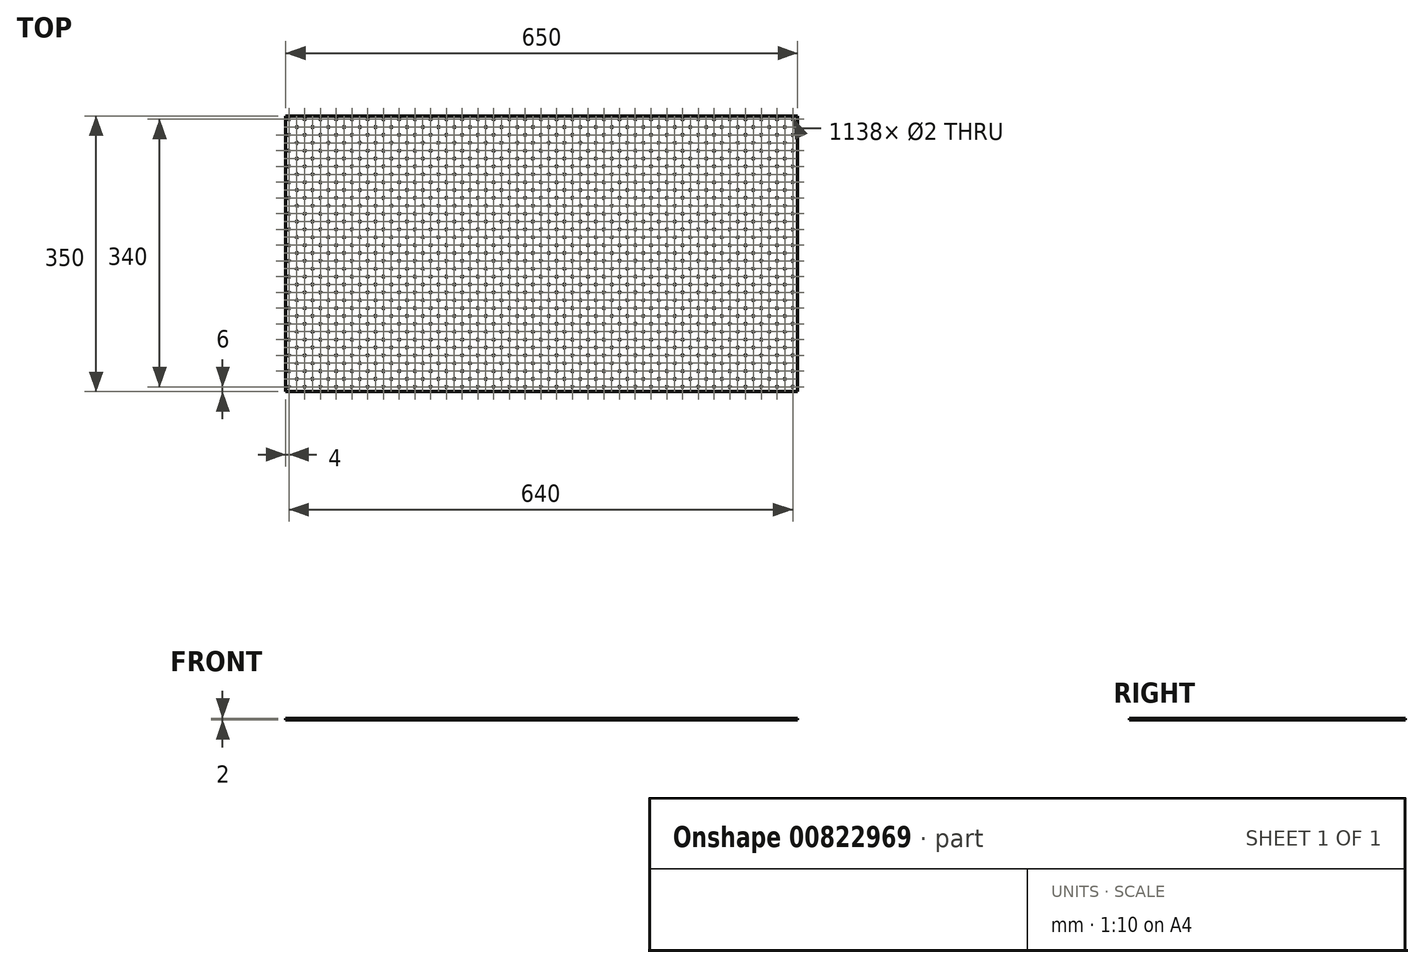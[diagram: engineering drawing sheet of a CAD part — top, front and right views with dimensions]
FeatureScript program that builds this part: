
annotation { "Feature Type Name" : "Feature", "Feature Type Description" : "" }
export const myFeature = defineFeature(function(context is Context, id is Id, definition is map)
    precondition{}
    {
        {
            var Q0;
            Q0=qCreatedBy(makeId("Top.planeOp"),FACE);
            var sketch = newSketch(context, id + "F0", { "sketchPlane" : qUnion([Q0])});
            skLineSegment(sketch, "E0.bottom", {"start": v(-325, -175) * mm, "end": v(325, -175) * mm});
            skLineSegment(sketch, "E0.top", {"start": v(-325, 175) * mm, "end": v(325, 175) * mm});
            skLineSegment(sketch, "E0.left", {"start": v(-325, -175) * mm, "end": v(-325, 175) * mm});
            skLineSegment(sketch, "E0.right", {"start": v(325, -175) * mm, "end": v(325, 175) * mm});
            skPoint(sketch, "E0.middle", {"position": v(0, 0) * mm});
            skCircle(sketch, "E1", {"center": v(-321, 171) * mm, "radius": 1 * mm});
            skCircle(sketch, "E2", {"center": v(-311, 161) * mm, "radius": 1 * mm});
            skCircle(sketch, "E3.0.1.0", {"center": v(-321, 151) * mm, "radius": 1 * mm});
            skCircle(sketch, "E3.0.1.1", {"center": v(-311, 141) * mm, "radius": 1 * mm});
            skCircle(sketch, "E3.0.2.0", {"center": v(-321, 131) * mm, "radius": 1 * mm});
            skCircle(sketch, "E3.0.2.1", {"center": v(-311, 121) * mm, "radius": 1 * mm});
            skCircle(sketch, "E3.0.3.0", {"center": v(-321, 111) * mm, "radius": 1 * mm});
            skCircle(sketch, "E3.0.3.1", {"center": v(-311, 101) * mm, "radius": 1 * mm});
            skCircle(sketch, "E3.0.4.0", {"center": v(-321, 91) * mm, "radius": 1 * mm});
            skCircle(sketch, "E3.0.4.1", {"center": v(-311, 81) * mm, "radius": 1 * mm});
            skCircle(sketch, "E3.0.5.0", {"center": v(-321, 71) * mm, "radius": 1 * mm});
            skCircle(sketch, "E3.0.5.1", {"center": v(-311, 61) * mm, "radius": 1 * mm});
            skCircle(sketch, "E3.0.6.0", {"center": v(-321, 51) * mm, "radius": 1 * mm});
            skCircle(sketch, "E3.0.6.1", {"center": v(-311, 41) * mm, "radius": 1 * mm});
            skCircle(sketch, "E3.0.7.0", {"center": v(-321, 31) * mm, "radius": 1 * mm});
            skCircle(sketch, "E3.0.7.1", {"center": v(-311, 21) * mm, "radius": 1 * mm});
            skCircle(sketch, "E3.0.8.0", {"center": v(-321, 11) * mm, "radius": 1 * mm});
            skCircle(sketch, "E3.0.8.1", {"center": v(-311, 1) * mm, "radius": 1 * mm});
            skCircle(sketch, "E3.0.9.0", {"center": v(-321, -9) * mm, "radius": 1 * mm});
            skCircle(sketch, "E3.0.9.1", {"center": v(-311, -19) * mm, "radius": 1 * mm});
            skCircle(sketch, "E3.0.10.0", {"center": v(-321, -29) * mm, "radius": 1 * mm});
            skCircle(sketch, "E3.0.10.1", {"center": v(-311, -39) * mm, "radius": 1 * mm});
            skCircle(sketch, "E3.0.11.0", {"center": v(-321, -49) * mm, "radius": 1 * mm});
            skCircle(sketch, "E3.0.11.1", {"center": v(-311, -59) * mm, "radius": 1 * mm});
            skCircle(sketch, "E3.0.12.0", {"center": v(-321, -69) * mm, "radius": 1 * mm});
            skCircle(sketch, "E3.0.12.1", {"center": v(-311, -79) * mm, "radius": 1 * mm});
            skCircle(sketch, "E3.0.13.0", {"center": v(-321, -89) * mm, "radius": 1 * mm});
            skCircle(sketch, "E3.0.13.1", {"center": v(-311, -99) * mm, "radius": 1 * mm});
            skCircle(sketch, "E3.0.14.0", {"center": v(-321, -109) * mm, "radius": 1 * mm});
            skCircle(sketch, "E3.0.14.1", {"center": v(-311, -119) * mm, "radius": 1 * mm});
            skCircle(sketch, "E3.0.15.0", {"center": v(-321, -129) * mm, "radius": 1 * mm});
            skCircle(sketch, "E3.0.15.1", {"center": v(-311, -139) * mm, "radius": 1 * mm});
            skCircle(sketch, "E3.0.16.0", {"center": v(-321, -149) * mm, "radius": 1 * mm});
            skCircle(sketch, "E3.0.16.1", {"center": v(-311, -159) * mm, "radius": 1 * mm});
            skCircle(sketch, "E3.0.17.0", {"center": v(-321, -169) * mm, "radius": 1 * mm});
            skCircle(sketch, "E3.0.17.1", {"center": v(-311, -179) * mm, "radius": 1 * mm, "construction": true});
            skCircle(sketch, "E3.1.0.0", {"center": v(-301, 171) * mm, "radius": 1 * mm});
            skCircle(sketch, "E3.1.0.1", {"center": v(-291, 161) * mm, "radius": 1 * mm});
            skCircle(sketch, "E3.1.1.0", {"center": v(-301, 151) * mm, "radius": 1 * mm});
            skCircle(sketch, "E3.1.1.1", {"center": v(-291, 141) * mm, "radius": 1 * mm});
            skCircle(sketch, "E3.1.2.0", {"center": v(-301, 131) * mm, "radius": 1 * mm});
            skCircle(sketch, "E3.1.2.1", {"center": v(-291, 121) * mm, "radius": 1 * mm});
            skCircle(sketch, "E3.1.3.0", {"center": v(-301, 111) * mm, "radius": 1 * mm});
            skCircle(sketch, "E3.1.3.1", {"center": v(-291, 101) * mm, "radius": 1 * mm});
            skCircle(sketch, "E3.1.4.0", {"center": v(-301, 91) * mm, "radius": 1 * mm});
            skCircle(sketch, "E3.1.4.1", {"center": v(-291, 81) * mm, "radius": 1 * mm});
            skCircle(sketch, "E3.1.5.0", {"center": v(-301, 71) * mm, "radius": 1 * mm});
            skCircle(sketch, "E3.1.5.1", {"center": v(-291, 61) * mm, "radius": 1 * mm});
            skCircle(sketch, "E3.1.6.0", {"center": v(-301, 51) * mm, "radius": 1 * mm});
            skCircle(sketch, "E3.1.6.1", {"center": v(-291, 41) * mm, "radius": 1 * mm});
            skCircle(sketch, "E3.1.7.0", {"center": v(-301, 31) * mm, "radius": 1 * mm});
            skCircle(sketch, "E3.1.7.1", {"center": v(-291, 21) * mm, "radius": 1 * mm});
            skCircle(sketch, "E3.1.8.0", {"center": v(-301, 11) * mm, "radius": 1 * mm});
            skCircle(sketch, "E3.1.8.1", {"center": v(-291, 1) * mm, "radius": 1 * mm});
            skCircle(sketch, "E3.1.9.0", {"center": v(-301, -9) * mm, "radius": 1 * mm});
            skCircle(sketch, "E3.1.9.1", {"center": v(-291, -19) * mm, "radius": 1 * mm});
            skCircle(sketch, "E3.1.10.0", {"center": v(-301, -29) * mm, "radius": 1 * mm});
            skCircle(sketch, "E3.1.10.1", {"center": v(-291, -39) * mm, "radius": 1 * mm});
            skCircle(sketch, "E3.1.11.0", {"center": v(-301, -49) * mm, "radius": 1 * mm});
            skCircle(sketch, "E3.1.11.1", {"center": v(-291, -59) * mm, "radius": 1 * mm});
            skCircle(sketch, "E3.1.12.0", {"center": v(-301, -69) * mm, "radius": 1 * mm});
            skCircle(sketch, "E3.1.12.1", {"center": v(-291, -79) * mm, "radius": 1 * mm});
            skCircle(sketch, "E3.1.13.0", {"center": v(-301, -89) * mm, "radius": 1 * mm});
            skCircle(sketch, "E3.1.13.1", {"center": v(-291, -99) * mm, "radius": 1 * mm});
            skCircle(sketch, "E3.1.14.0", {"center": v(-301, -109) * mm, "radius": 1 * mm});
            skCircle(sketch, "E3.1.14.1", {"center": v(-291, -119) * mm, "radius": 1 * mm});
            skCircle(sketch, "E3.1.15.0", {"center": v(-301, -129) * mm, "radius": 1 * mm});
            skCircle(sketch, "E3.1.15.1", {"center": v(-291, -139) * mm, "radius": 1 * mm});
            skCircle(sketch, "E3.1.16.0", {"center": v(-301, -149) * mm, "radius": 1 * mm});
            skCircle(sketch, "E3.1.16.1", {"center": v(-291, -159) * mm, "radius": 1 * mm});
            skCircle(sketch, "E3.1.17.0", {"center": v(-301, -169) * mm, "radius": 1 * mm});
            skCircle(sketch, "E3.1.17.1", {"center": v(-291, -179) * mm, "radius": 1 * mm, "construction": true});
            skCircle(sketch, "E3.2.0.0", {"center": v(-281, 171) * mm, "radius": 1 * mm});
            skCircle(sketch, "E3.2.0.1", {"center": v(-271, 161) * mm, "radius": 1 * mm});
            skCircle(sketch, "E3.2.1.0", {"center": v(-281, 151) * mm, "radius": 1 * mm});
            skCircle(sketch, "E3.2.1.1", {"center": v(-271, 141) * mm, "radius": 1 * mm});
            skCircle(sketch, "E3.2.2.0", {"center": v(-281, 131) * mm, "radius": 1 * mm});
            skCircle(sketch, "E3.2.2.1", {"center": v(-271, 121) * mm, "radius": 1 * mm});
            skCircle(sketch, "E3.2.3.0", {"center": v(-281, 111) * mm, "radius": 1 * mm});
            skCircle(sketch, "E3.2.3.1", {"center": v(-271, 101) * mm, "radius": 1 * mm});
            skCircle(sketch, "E3.2.4.0", {"center": v(-281, 91) * mm, "radius": 1 * mm});
            skCircle(sketch, "E3.2.4.1", {"center": v(-271, 81) * mm, "radius": 1 * mm});
            skCircle(sketch, "E3.2.5.0", {"center": v(-281, 71) * mm, "radius": 1 * mm});
            skCircle(sketch, "E3.2.5.1", {"center": v(-271, 61) * mm, "radius": 1 * mm});
            skCircle(sketch, "E3.2.6.0", {"center": v(-281, 51) * mm, "radius": 1 * mm});
            skCircle(sketch, "E3.2.6.1", {"center": v(-271, 41) * mm, "radius": 1 * mm});
            skCircle(sketch, "E3.2.7.0", {"center": v(-281, 31) * mm, "radius": 1 * mm});
            skCircle(sketch, "E3.2.7.1", {"center": v(-271, 21) * mm, "radius": 1 * mm});
            skCircle(sketch, "E3.2.8.0", {"center": v(-281, 11) * mm, "radius": 1 * mm});
            skCircle(sketch, "E3.2.8.1", {"center": v(-271, 1) * mm, "radius": 1 * mm});
            skCircle(sketch, "E3.2.9.0", {"center": v(-281, -9) * mm, "radius": 1 * mm});
            skCircle(sketch, "E3.2.9.1", {"center": v(-271, -19) * mm, "radius": 1 * mm});
            skCircle(sketch, "E3.2.10.0", {"center": v(-281, -29) * mm, "radius": 1 * mm});
            skCircle(sketch, "E3.2.10.1", {"center": v(-271, -39) * mm, "radius": 1 * mm});
            skCircle(sketch, "E3.2.11.0", {"center": v(-281, -49) * mm, "radius": 1 * mm});
            skCircle(sketch, "E3.2.11.1", {"center": v(-271, -59) * mm, "radius": 1 * mm});
            skCircle(sketch, "E3.2.12.0", {"center": v(-281, -69) * mm, "radius": 1 * mm});
            skCircle(sketch, "E3.2.12.1", {"center": v(-271, -79) * mm, "radius": 1 * mm});
            skCircle(sketch, "E3.2.13.0", {"center": v(-281, -89) * mm, "radius": 1 * mm});
            skCircle(sketch, "E3.2.13.1", {"center": v(-271, -99) * mm, "radius": 1 * mm});
            skCircle(sketch, "E3.2.14.0", {"center": v(-281, -109) * mm, "radius": 1 * mm});
            skCircle(sketch, "E3.2.14.1", {"center": v(-271, -119) * mm, "radius": 1 * mm});
            skCircle(sketch, "E3.2.15.0", {"center": v(-281, -129) * mm, "radius": 1 * mm});
            skCircle(sketch, "E3.2.15.1", {"center": v(-271, -139) * mm, "radius": 1 * mm});
            skCircle(sketch, "E3.2.16.0", {"center": v(-281, -149) * mm, "radius": 1 * mm});
            skCircle(sketch, "E3.2.16.1", {"center": v(-271, -159) * mm, "radius": 1 * mm});
            skCircle(sketch, "E3.2.17.0", {"center": v(-281, -169) * mm, "radius": 1 * mm});
            skCircle(sketch, "E3.2.17.1", {"center": v(-271, -179) * mm, "radius": 1 * mm, "construction": true});
            skCircle(sketch, "E3.3.0.0", {"center": v(-261, 171) * mm, "radius": 1 * mm});
            skCircle(sketch, "E3.3.0.1", {"center": v(-251, 161) * mm, "radius": 1 * mm});
            skCircle(sketch, "E3.3.1.0", {"center": v(-261, 151) * mm, "radius": 1 * mm});
            skCircle(sketch, "E3.3.1.1", {"center": v(-251, 141) * mm, "radius": 1 * mm});
            skCircle(sketch, "E3.3.2.0", {"center": v(-261, 131) * mm, "radius": 1 * mm});
            skCircle(sketch, "E3.3.2.1", {"center": v(-251, 121) * mm, "radius": 1 * mm});
            skCircle(sketch, "E3.3.3.0", {"center": v(-261, 111) * mm, "radius": 1 * mm});
            skCircle(sketch, "E3.3.3.1", {"center": v(-251, 101) * mm, "radius": 1 * mm});
            skCircle(sketch, "E3.3.4.0", {"center": v(-261, 91) * mm, "radius": 1 * mm});
            skCircle(sketch, "E3.3.4.1", {"center": v(-251, 81) * mm, "radius": 1 * mm});
            skCircle(sketch, "E3.3.5.0", {"center": v(-261, 71) * mm, "radius": 1 * mm});
            skCircle(sketch, "E3.3.5.1", {"center": v(-251, 61) * mm, "radius": 1 * mm});
            skCircle(sketch, "E3.3.6.0", {"center": v(-261, 51) * mm, "radius": 1 * mm});
            skCircle(sketch, "E3.3.6.1", {"center": v(-251, 41) * mm, "radius": 1 * mm});
            skCircle(sketch, "E3.3.7.0", {"center": v(-261, 31) * mm, "radius": 1 * mm});
            skCircle(sketch, "E3.3.7.1", {"center": v(-251, 21) * mm, "radius": 1 * mm});
            skCircle(sketch, "E3.3.8.0", {"center": v(-261, 11) * mm, "radius": 1 * mm});
            skCircle(sketch, "E3.3.8.1", {"center": v(-251, 1) * mm, "radius": 1 * mm});
            skCircle(sketch, "E3.3.9.0", {"center": v(-261, -9) * mm, "radius": 1 * mm});
            skCircle(sketch, "E3.3.9.1", {"center": v(-251, -19) * mm, "radius": 1 * mm});
            skCircle(sketch, "E3.3.10.0", {"center": v(-261, -29) * mm, "radius": 1 * mm});
            skCircle(sketch, "E3.3.10.1", {"center": v(-251, -39) * mm, "radius": 1 * mm});
            skCircle(sketch, "E3.3.11.0", {"center": v(-261, -49) * mm, "radius": 1 * mm});
            skCircle(sketch, "E3.3.11.1", {"center": v(-251, -59) * mm, "radius": 1 * mm});
            skCircle(sketch, "E3.3.12.0", {"center": v(-261, -69) * mm, "radius": 1 * mm});
            skCircle(sketch, "E3.3.12.1", {"center": v(-251, -79) * mm, "radius": 1 * mm});
            skCircle(sketch, "E3.3.13.0", {"center": v(-261, -89) * mm, "radius": 1 * mm});
            skCircle(sketch, "E3.3.13.1", {"center": v(-251, -99) * mm, "radius": 1 * mm});
            skCircle(sketch, "E3.3.14.0", {"center": v(-261, -109) * mm, "radius": 1 * mm});
            skCircle(sketch, "E3.3.14.1", {"center": v(-251, -119) * mm, "radius": 1 * mm});
            skCircle(sketch, "E3.3.15.0", {"center": v(-261, -129) * mm, "radius": 1 * mm});
            skCircle(sketch, "E3.3.15.1", {"center": v(-251, -139) * mm, "radius": 1 * mm});
            skCircle(sketch, "E3.3.16.0", {"center": v(-261, -149) * mm, "radius": 1 * mm});
            skCircle(sketch, "E3.3.16.1", {"center": v(-251, -159) * mm, "radius": 1 * mm});
            skCircle(sketch, "E3.3.17.0", {"center": v(-261, -169) * mm, "radius": 1 * mm});
            skCircle(sketch, "E3.3.17.1", {"center": v(-251, -179) * mm, "radius": 1 * mm, "construction": true});
            skCircle(sketch, "E3.4.0.0", {"center": v(-241, 171) * mm, "radius": 1 * mm});
            skCircle(sketch, "E3.4.0.1", {"center": v(-231, 161) * mm, "radius": 1 * mm});
            skCircle(sketch, "E3.4.1.0", {"center": v(-241, 151) * mm, "radius": 1 * mm});
            skCircle(sketch, "E3.4.1.1", {"center": v(-231, 141) * mm, "radius": 1 * mm});
            skCircle(sketch, "E3.4.2.0", {"center": v(-241, 131) * mm, "radius": 1 * mm});
            skCircle(sketch, "E3.4.2.1", {"center": v(-231, 121) * mm, "radius": 1 * mm});
            skCircle(sketch, "E3.4.3.0", {"center": v(-241, 111) * mm, "radius": 1 * mm});
            skCircle(sketch, "E3.4.3.1", {"center": v(-231, 101) * mm, "radius": 1 * mm});
            skCircle(sketch, "E3.4.4.0", {"center": v(-241, 91) * mm, "radius": 1 * mm});
            skCircle(sketch, "E3.4.4.1", {"center": v(-231, 81) * mm, "radius": 1 * mm});
            skCircle(sketch, "E3.4.5.0", {"center": v(-241, 71) * mm, "radius": 1 * mm});
            skCircle(sketch, "E3.4.5.1", {"center": v(-231, 61) * mm, "radius": 1 * mm});
            skCircle(sketch, "E3.4.6.0", {"center": v(-241, 51) * mm, "radius": 1 * mm});
            skCircle(sketch, "E3.4.6.1", {"center": v(-231, 41) * mm, "radius": 1 * mm});
            skCircle(sketch, "E3.4.7.0", {"center": v(-241, 31) * mm, "radius": 1 * mm});
            skCircle(sketch, "E3.4.7.1", {"center": v(-231, 21) * mm, "radius": 1 * mm});
            skCircle(sketch, "E3.4.8.0", {"center": v(-241, 11) * mm, "radius": 1 * mm});
            skCircle(sketch, "E3.4.8.1", {"center": v(-231, 1) * mm, "radius": 1 * mm});
            skCircle(sketch, "E3.4.9.0", {"center": v(-241, -9) * mm, "radius": 1 * mm});
            skCircle(sketch, "E3.4.9.1", {"center": v(-231, -19) * mm, "radius": 1 * mm});
            skCircle(sketch, "E3.4.10.0", {"center": v(-241, -29) * mm, "radius": 1 * mm});
            skCircle(sketch, "E3.4.10.1", {"center": v(-231, -39) * mm, "radius": 1 * mm});
            skCircle(sketch, "E3.4.11.0", {"center": v(-241, -49) * mm, "radius": 1 * mm});
            skCircle(sketch, "E3.4.11.1", {"center": v(-231, -59) * mm, "radius": 1 * mm});
            skCircle(sketch, "E3.4.12.0", {"center": v(-241, -69) * mm, "radius": 1 * mm});
            skCircle(sketch, "E3.4.12.1", {"center": v(-231, -79) * mm, "radius": 1 * mm});
            skCircle(sketch, "E3.4.13.0", {"center": v(-241, -89) * mm, "radius": 1 * mm});
            skCircle(sketch, "E3.4.13.1", {"center": v(-231, -99) * mm, "radius": 1 * mm});
            skCircle(sketch, "E3.4.14.0", {"center": v(-241, -109) * mm, "radius": 1 * mm});
            skCircle(sketch, "E3.4.14.1", {"center": v(-231, -119) * mm, "radius": 1 * mm});
            skCircle(sketch, "E3.4.15.0", {"center": v(-241, -129) * mm, "radius": 1 * mm});
            skCircle(sketch, "E3.4.15.1", {"center": v(-231, -139) * mm, "radius": 1 * mm});
            skCircle(sketch, "E3.4.16.0", {"center": v(-241, -149) * mm, "radius": 1 * mm});
            skCircle(sketch, "E3.4.16.1", {"center": v(-231, -159) * mm, "radius": 1 * mm});
            skCircle(sketch, "E3.4.17.0", {"center": v(-241, -169) * mm, "radius": 1 * mm});
            skCircle(sketch, "E3.4.17.1", {"center": v(-231, -179) * mm, "radius": 1 * mm, "construction": true});
            skCircle(sketch, "E3.5.0.0", {"center": v(-221, 171) * mm, "radius": 1 * mm});
            skCircle(sketch, "E3.5.0.1", {"center": v(-211, 161) * mm, "radius": 1 * mm});
            skCircle(sketch, "E3.5.1.0", {"center": v(-221, 151) * mm, "radius": 1 * mm});
            skCircle(sketch, "E3.5.1.1", {"center": v(-211, 141) * mm, "radius": 1 * mm});
            skCircle(sketch, "E3.5.2.0", {"center": v(-221, 131) * mm, "radius": 1 * mm});
            skCircle(sketch, "E3.5.2.1", {"center": v(-211, 121) * mm, "radius": 1 * mm});
            skCircle(sketch, "E3.5.3.0", {"center": v(-221, 111) * mm, "radius": 1 * mm});
            skCircle(sketch, "E3.5.3.1", {"center": v(-211, 101) * mm, "radius": 1 * mm});
            skCircle(sketch, "E3.5.4.0", {"center": v(-221, 91) * mm, "radius": 1 * mm});
            skCircle(sketch, "E3.5.4.1", {"center": v(-211, 81) * mm, "radius": 1 * mm});
            skCircle(sketch, "E3.5.5.0", {"center": v(-221, 71) * mm, "radius": 1 * mm});
            skCircle(sketch, "E3.5.5.1", {"center": v(-211, 61) * mm, "radius": 1 * mm});
            skCircle(sketch, "E3.5.6.0", {"center": v(-221, 51) * mm, "radius": 1 * mm});
            skCircle(sketch, "E3.5.6.1", {"center": v(-211, 41) * mm, "radius": 1 * mm});
            skCircle(sketch, "E3.5.7.0", {"center": v(-221, 31) * mm, "radius": 1 * mm});
            skCircle(sketch, "E3.5.7.1", {"center": v(-211, 21) * mm, "radius": 1 * mm});
            skCircle(sketch, "E3.5.8.0", {"center": v(-221, 11) * mm, "radius": 1 * mm});
            skCircle(sketch, "E3.5.8.1", {"center": v(-211, 1) * mm, "radius": 1 * mm});
            skCircle(sketch, "E3.5.9.0", {"center": v(-221, -9) * mm, "radius": 1 * mm});
            skCircle(sketch, "E3.5.9.1", {"center": v(-211, -19) * mm, "radius": 1 * mm});
            skCircle(sketch, "E3.5.10.0", {"center": v(-221, -29) * mm, "radius": 1 * mm});
            skCircle(sketch, "E3.5.10.1", {"center": v(-211, -39) * mm, "radius": 1 * mm});
            skCircle(sketch, "E3.5.11.0", {"center": v(-221, -49) * mm, "radius": 1 * mm});
            skCircle(sketch, "E3.5.11.1", {"center": v(-211, -59) * mm, "radius": 1 * mm});
            skCircle(sketch, "E3.5.12.0", {"center": v(-221, -69) * mm, "radius": 1 * mm});
            skCircle(sketch, "E3.5.12.1", {"center": v(-211, -79) * mm, "radius": 1 * mm});
            skCircle(sketch, "E3.5.13.0", {"center": v(-221, -89) * mm, "radius": 1 * mm});
            skCircle(sketch, "E3.5.13.1", {"center": v(-211, -99) * mm, "radius": 1 * mm});
            skCircle(sketch, "E3.5.14.0", {"center": v(-221, -109) * mm, "radius": 1 * mm});
            skCircle(sketch, "E3.5.14.1", {"center": v(-211, -119) * mm, "radius": 1 * mm});
            skCircle(sketch, "E3.5.15.0", {"center": v(-221, -129) * mm, "radius": 1 * mm});
            skCircle(sketch, "E3.5.15.1", {"center": v(-211, -139) * mm, "radius": 1 * mm});
            skCircle(sketch, "E3.5.16.0", {"center": v(-221, -149) * mm, "radius": 1 * mm});
            skCircle(sketch, "E3.5.16.1", {"center": v(-211, -159) * mm, "radius": 1 * mm});
            skCircle(sketch, "E3.5.17.0", {"center": v(-221, -169) * mm, "radius": 1 * mm});
            skCircle(sketch, "E3.5.17.1", {"center": v(-211, -179) * mm, "radius": 1 * mm, "construction": true});
            skCircle(sketch, "E3.6.0.0", {"center": v(-201, 171) * mm, "radius": 1 * mm});
            skCircle(sketch, "E3.6.0.1", {"center": v(-191, 161) * mm, "radius": 1 * mm});
            skCircle(sketch, "E3.6.1.0", {"center": v(-201, 151) * mm, "radius": 1 * mm});
            skCircle(sketch, "E3.6.1.1", {"center": v(-191, 141) * mm, "radius": 1 * mm});
            skCircle(sketch, "E3.6.2.0", {"center": v(-201, 131) * mm, "radius": 1 * mm});
            skCircle(sketch, "E3.6.2.1", {"center": v(-191, 121) * mm, "radius": 1 * mm});
            skCircle(sketch, "E3.6.3.0", {"center": v(-201, 111) * mm, "radius": 1 * mm});
            skCircle(sketch, "E3.6.3.1", {"center": v(-191, 101) * mm, "radius": 1 * mm});
            skCircle(sketch, "E3.6.4.0", {"center": v(-201, 91) * mm, "radius": 1 * mm});
            skCircle(sketch, "E3.6.4.1", {"center": v(-191, 81) * mm, "radius": 1 * mm});
            skCircle(sketch, "E3.6.5.0", {"center": v(-201, 71) * mm, "radius": 1 * mm});
            skCircle(sketch, "E3.6.5.1", {"center": v(-191, 61) * mm, "radius": 1 * mm});
            skCircle(sketch, "E3.6.6.0", {"center": v(-201, 51) * mm, "radius": 1 * mm});
            skCircle(sketch, "E3.6.6.1", {"center": v(-191, 41) * mm, "radius": 1 * mm});
            skCircle(sketch, "E3.6.7.0", {"center": v(-201, 31) * mm, "radius": 1 * mm});
            skCircle(sketch, "E3.6.7.1", {"center": v(-191, 21) * mm, "radius": 1 * mm});
            skCircle(sketch, "E3.6.8.0", {"center": v(-201, 11) * mm, "radius": 1 * mm});
            skCircle(sketch, "E3.6.8.1", {"center": v(-191, 1) * mm, "radius": 1 * mm});
            skCircle(sketch, "E3.6.9.0", {"center": v(-201, -9) * mm, "radius": 1 * mm});
            skCircle(sketch, "E3.6.9.1", {"center": v(-191, -19) * mm, "radius": 1 * mm});
            skCircle(sketch, "E3.6.10.0", {"center": v(-201, -29) * mm, "radius": 1 * mm});
            skCircle(sketch, "E3.6.10.1", {"center": v(-191, -39) * mm, "radius": 1 * mm});
            skCircle(sketch, "E3.6.11.0", {"center": v(-201, -49) * mm, "radius": 1 * mm});
            skCircle(sketch, "E3.6.11.1", {"center": v(-191, -59) * mm, "radius": 1 * mm});
            skCircle(sketch, "E3.6.12.0", {"center": v(-201, -69) * mm, "radius": 1 * mm});
            skCircle(sketch, "E3.6.12.1", {"center": v(-191, -79) * mm, "radius": 1 * mm});
            skCircle(sketch, "E3.6.13.0", {"center": v(-201, -89) * mm, "radius": 1 * mm});
            skCircle(sketch, "E3.6.13.1", {"center": v(-191, -99) * mm, "radius": 1 * mm});
            skCircle(sketch, "E3.6.14.0", {"center": v(-201, -109) * mm, "radius": 1 * mm});
            skCircle(sketch, "E3.6.14.1", {"center": v(-191, -119) * mm, "radius": 1 * mm});
            skCircle(sketch, "E3.6.15.0", {"center": v(-201, -129) * mm, "radius": 1 * mm});
            skCircle(sketch, "E3.6.15.1", {"center": v(-191, -139) * mm, "radius": 1 * mm});
            skCircle(sketch, "E3.6.16.0", {"center": v(-201, -149) * mm, "radius": 1 * mm});
            skCircle(sketch, "E3.6.16.1", {"center": v(-191, -159) * mm, "radius": 1 * mm});
            skCircle(sketch, "E3.6.17.0", {"center": v(-201, -169) * mm, "radius": 1 * mm});
            skCircle(sketch, "E3.6.17.1", {"center": v(-191, -179) * mm, "radius": 1 * mm, "construction": true});
            skCircle(sketch, "E3.7.0.0", {"center": v(-181, 171) * mm, "radius": 1 * mm});
            skCircle(sketch, "E3.7.0.1", {"center": v(-171, 161) * mm, "radius": 1 * mm});
            skCircle(sketch, "E3.7.1.0", {"center": v(-181, 151) * mm, "radius": 1 * mm});
            skCircle(sketch, "E3.7.1.1", {"center": v(-171, 141) * mm, "radius": 1 * mm});
            skCircle(sketch, "E3.7.2.0", {"center": v(-181, 131) * mm, "radius": 1 * mm});
            skCircle(sketch, "E3.7.2.1", {"center": v(-171, 121) * mm, "radius": 1 * mm});
            skCircle(sketch, "E3.7.3.0", {"center": v(-181, 111) * mm, "radius": 1 * mm});
            skCircle(sketch, "E3.7.3.1", {"center": v(-171, 101) * mm, "radius": 1 * mm});
            skCircle(sketch, "E3.7.4.0", {"center": v(-181, 91) * mm, "radius": 1 * mm});
            skCircle(sketch, "E3.7.4.1", {"center": v(-171, 81) * mm, "radius": 1 * mm});
            skCircle(sketch, "E3.7.5.0", {"center": v(-181, 71) * mm, "radius": 1 * mm});
            skCircle(sketch, "E3.7.5.1", {"center": v(-171, 61) * mm, "radius": 1 * mm});
            skCircle(sketch, "E3.7.6.0", {"center": v(-181, 51) * mm, "radius": 1 * mm});
            skCircle(sketch, "E3.7.6.1", {"center": v(-171, 41) * mm, "radius": 1 * mm});
            skCircle(sketch, "E3.7.7.0", {"center": v(-181, 31) * mm, "radius": 1 * mm});
            skCircle(sketch, "E3.7.7.1", {"center": v(-171, 21) * mm, "radius": 1 * mm});
            skCircle(sketch, "E3.7.8.0", {"center": v(-181, 11) * mm, "radius": 1 * mm});
            skCircle(sketch, "E3.7.8.1", {"center": v(-171, 1) * mm, "radius": 1 * mm});
            skCircle(sketch, "E3.7.9.0", {"center": v(-181, -9) * mm, "radius": 1 * mm});
            skCircle(sketch, "E3.7.9.1", {"center": v(-171, -19) * mm, "radius": 1 * mm});
            skCircle(sketch, "E3.7.10.0", {"center": v(-181, -29) * mm, "radius": 1 * mm});
            skCircle(sketch, "E3.7.10.1", {"center": v(-171, -39) * mm, "radius": 1 * mm});
            skCircle(sketch, "E3.7.11.0", {"center": v(-181, -49) * mm, "radius": 1 * mm});
            skCircle(sketch, "E3.7.11.1", {"center": v(-171, -59) * mm, "radius": 1 * mm});
            skCircle(sketch, "E3.7.12.0", {"center": v(-181, -69) * mm, "radius": 1 * mm});
            skCircle(sketch, "E3.7.12.1", {"center": v(-171, -79) * mm, "radius": 1 * mm});
            skCircle(sketch, "E3.7.13.0", {"center": v(-181, -89) * mm, "radius": 1 * mm});
            skCircle(sketch, "E3.7.13.1", {"center": v(-171, -99) * mm, "radius": 1 * mm});
            skCircle(sketch, "E3.7.14.0", {"center": v(-181, -109) * mm, "radius": 1 * mm});
            skCircle(sketch, "E3.7.14.1", {"center": v(-171, -119) * mm, "radius": 1 * mm});
            skCircle(sketch, "E3.7.15.0", {"center": v(-181, -129) * mm, "radius": 1 * mm});
            skCircle(sketch, "E3.7.15.1", {"center": v(-171, -139) * mm, "radius": 1 * mm});
            skCircle(sketch, "E3.7.16.0", {"center": v(-181, -149) * mm, "radius": 1 * mm});
            skCircle(sketch, "E3.7.16.1", {"center": v(-171, -159) * mm, "radius": 1 * mm});
            skCircle(sketch, "E3.7.17.0", {"center": v(-181, -169) * mm, "radius": 1 * mm});
            skCircle(sketch, "E3.7.17.1", {"center": v(-171, -179) * mm, "radius": 1 * mm, "construction": true});
            skCircle(sketch, "E3.8.0.0", {"center": v(-161, 171) * mm, "radius": 1 * mm});
            skCircle(sketch, "E3.8.0.1", {"center": v(-151, 161) * mm, "radius": 1 * mm});
            skCircle(sketch, "E3.8.1.0", {"center": v(-161, 151) * mm, "radius": 1 * mm});
            skCircle(sketch, "E3.8.1.1", {"center": v(-151, 141) * mm, "radius": 1 * mm});
            skCircle(sketch, "E3.8.2.0", {"center": v(-161, 131) * mm, "radius": 1 * mm});
            skCircle(sketch, "E3.8.2.1", {"center": v(-151, 121) * mm, "radius": 1 * mm});
            skCircle(sketch, "E3.8.3.0", {"center": v(-161, 111) * mm, "radius": 1 * mm});
            skCircle(sketch, "E3.8.3.1", {"center": v(-151, 101) * mm, "radius": 1 * mm});
            skCircle(sketch, "E3.8.4.0", {"center": v(-161, 91) * mm, "radius": 1 * mm});
            skCircle(sketch, "E3.8.4.1", {"center": v(-151, 81) * mm, "radius": 1 * mm});
            skCircle(sketch, "E3.8.5.0", {"center": v(-161, 71) * mm, "radius": 1 * mm});
            skCircle(sketch, "E3.8.5.1", {"center": v(-151, 61) * mm, "radius": 1 * mm});
            skCircle(sketch, "E3.8.6.0", {"center": v(-161, 51) * mm, "radius": 1 * mm});
            skCircle(sketch, "E3.8.6.1", {"center": v(-151, 41) * mm, "radius": 1 * mm});
            skCircle(sketch, "E3.8.7.0", {"center": v(-161, 31) * mm, "radius": 1 * mm});
            skCircle(sketch, "E3.8.7.1", {"center": v(-151, 21) * mm, "radius": 1 * mm});
            skCircle(sketch, "E3.8.8.0", {"center": v(-161, 11) * mm, "radius": 1 * mm});
            skCircle(sketch, "E3.8.8.1", {"center": v(-151, 1) * mm, "radius": 1 * mm});
            skCircle(sketch, "E3.8.9.0", {"center": v(-161, -9) * mm, "radius": 1 * mm});
            skCircle(sketch, "E3.8.9.1", {"center": v(-151, -19) * mm, "radius": 1 * mm});
            skCircle(sketch, "E3.8.10.0", {"center": v(-161, -29) * mm, "radius": 1 * mm});
            skCircle(sketch, "E3.8.10.1", {"center": v(-151, -39) * mm, "radius": 1 * mm});
            skCircle(sketch, "E3.8.11.0", {"center": v(-161, -49) * mm, "radius": 1 * mm});
            skCircle(sketch, "E3.8.11.1", {"center": v(-151, -59) * mm, "radius": 1 * mm});
            skCircle(sketch, "E3.8.12.0", {"center": v(-161, -69) * mm, "radius": 1 * mm});
            skCircle(sketch, "E3.8.12.1", {"center": v(-151, -79) * mm, "radius": 1 * mm});
            skCircle(sketch, "E3.8.13.0", {"center": v(-161, -89) * mm, "radius": 1 * mm});
            skCircle(sketch, "E3.8.13.1", {"center": v(-151, -99) * mm, "radius": 1 * mm});
            skCircle(sketch, "E3.8.14.0", {"center": v(-161, -109) * mm, "radius": 1 * mm});
            skCircle(sketch, "E3.8.14.1", {"center": v(-151, -119) * mm, "radius": 1 * mm});
            skCircle(sketch, "E3.8.15.0", {"center": v(-161, -129) * mm, "radius": 1 * mm});
            skCircle(sketch, "E3.8.15.1", {"center": v(-151, -139) * mm, "radius": 1 * mm});
            skCircle(sketch, "E3.8.16.0", {"center": v(-161, -149) * mm, "radius": 1 * mm});
            skCircle(sketch, "E3.8.16.1", {"center": v(-151, -159) * mm, "radius": 1 * mm});
            skCircle(sketch, "E3.8.17.0", {"center": v(-161, -169) * mm, "radius": 1 * mm});
            skCircle(sketch, "E3.8.17.1", {"center": v(-151, -179) * mm, "radius": 1 * mm, "construction": true});
            skCircle(sketch, "E3.9.0.0", {"center": v(-141, 171) * mm, "radius": 1 * mm});
            skCircle(sketch, "E3.9.0.1", {"center": v(-131, 161) * mm, "radius": 1 * mm});
            skCircle(sketch, "E3.9.1.0", {"center": v(-141, 151) * mm, "radius": 1 * mm});
            skCircle(sketch, "E3.9.1.1", {"center": v(-131, 141) * mm, "radius": 1 * mm});
            skCircle(sketch, "E3.9.2.0", {"center": v(-141, 131) * mm, "radius": 1 * mm});
            skCircle(sketch, "E3.9.2.1", {"center": v(-131, 121) * mm, "radius": 1 * mm});
            skCircle(sketch, "E3.9.3.0", {"center": v(-141, 111) * mm, "radius": 1 * mm});
            skCircle(sketch, "E3.9.3.1", {"center": v(-131, 101) * mm, "radius": 1 * mm});
            skCircle(sketch, "E3.9.4.0", {"center": v(-141, 91) * mm, "radius": 1 * mm});
            skCircle(sketch, "E3.9.4.1", {"center": v(-131, 81) * mm, "radius": 1 * mm});
            skCircle(sketch, "E3.9.5.0", {"center": v(-141, 71) * mm, "radius": 1 * mm});
            skCircle(sketch, "E3.9.5.1", {"center": v(-131, 61) * mm, "radius": 1 * mm});
            skCircle(sketch, "E3.9.6.0", {"center": v(-141, 51) * mm, "radius": 1 * mm});
            skCircle(sketch, "E3.9.6.1", {"center": v(-131, 41) * mm, "radius": 1 * mm});
            skCircle(sketch, "E3.9.7.0", {"center": v(-141, 31) * mm, "radius": 1 * mm});
            skCircle(sketch, "E3.9.7.1", {"center": v(-131, 21) * mm, "radius": 1 * mm});
            skCircle(sketch, "E3.9.8.0", {"center": v(-141, 11) * mm, "radius": 1 * mm});
            skCircle(sketch, "E3.9.8.1", {"center": v(-131, 1) * mm, "radius": 1 * mm});
            skCircle(sketch, "E3.9.9.0", {"center": v(-141, -9) * mm, "radius": 1 * mm});
            skCircle(sketch, "E3.9.9.1", {"center": v(-131, -19) * mm, "radius": 1 * mm});
            skCircle(sketch, "E3.9.10.0", {"center": v(-141, -29) * mm, "radius": 1 * mm});
            skCircle(sketch, "E3.9.10.1", {"center": v(-131, -39) * mm, "radius": 1 * mm});
            skCircle(sketch, "E3.9.11.0", {"center": v(-141, -49) * mm, "radius": 1 * mm});
            skCircle(sketch, "E3.9.11.1", {"center": v(-131, -59) * mm, "radius": 1 * mm});
            skCircle(sketch, "E3.9.12.0", {"center": v(-141, -69) * mm, "radius": 1 * mm});
            skCircle(sketch, "E3.9.12.1", {"center": v(-131, -79) * mm, "radius": 1 * mm});
            skCircle(sketch, "E3.9.13.0", {"center": v(-141, -89) * mm, "radius": 1 * mm});
            skCircle(sketch, "E3.9.13.1", {"center": v(-131, -99) * mm, "radius": 1 * mm});
            skCircle(sketch, "E3.9.14.0", {"center": v(-141, -109) * mm, "radius": 1 * mm});
            skCircle(sketch, "E3.9.14.1", {"center": v(-131, -119) * mm, "radius": 1 * mm});
            skCircle(sketch, "E3.9.15.0", {"center": v(-141, -129) * mm, "radius": 1 * mm});
            skCircle(sketch, "E3.9.15.1", {"center": v(-131, -139) * mm, "radius": 1 * mm});
            skCircle(sketch, "E3.9.16.0", {"center": v(-141, -149) * mm, "radius": 1 * mm});
            skCircle(sketch, "E3.9.16.1", {"center": v(-131, -159) * mm, "radius": 1 * mm});
            skCircle(sketch, "E3.9.17.0", {"center": v(-141, -169) * mm, "radius": 1 * mm});
            skCircle(sketch, "E3.9.17.1", {"center": v(-131, -179) * mm, "radius": 1 * mm, "construction": true});
            skCircle(sketch, "E3.10.0.0", {"center": v(-121, 171) * mm, "radius": 1 * mm});
            skCircle(sketch, "E3.10.0.1", {"center": v(-111, 161) * mm, "radius": 1 * mm});
            skCircle(sketch, "E3.10.1.0", {"center": v(-121, 151) * mm, "radius": 1 * mm});
            skCircle(sketch, "E3.10.1.1", {"center": v(-111, 141) * mm, "radius": 1 * mm});
            skCircle(sketch, "E3.10.2.0", {"center": v(-121, 131) * mm, "radius": 1 * mm});
            skCircle(sketch, "E3.10.2.1", {"center": v(-111, 121) * mm, "radius": 1 * mm});
            skCircle(sketch, "E3.10.3.0", {"center": v(-121, 111) * mm, "radius": 1 * mm});
            skCircle(sketch, "E3.10.3.1", {"center": v(-111, 101) * mm, "radius": 1 * mm});
            skCircle(sketch, "E3.10.4.0", {"center": v(-121, 91) * mm, "radius": 1 * mm});
            skCircle(sketch, "E3.10.4.1", {"center": v(-111, 81) * mm, "radius": 1 * mm});
            skCircle(sketch, "E3.10.5.0", {"center": v(-121, 71) * mm, "radius": 1 * mm});
            skCircle(sketch, "E3.10.5.1", {"center": v(-111, 61) * mm, "radius": 1 * mm});
            skCircle(sketch, "E3.10.6.0", {"center": v(-121, 51) * mm, "radius": 1 * mm});
            skCircle(sketch, "E3.10.6.1", {"center": v(-111, 41) * mm, "radius": 1 * mm});
            skCircle(sketch, "E3.10.7.0", {"center": v(-121, 31) * mm, "radius": 1 * mm});
            skCircle(sketch, "E3.10.7.1", {"center": v(-111, 21) * mm, "radius": 1 * mm});
            skCircle(sketch, "E3.10.8.0", {"center": v(-121, 11) * mm, "radius": 1 * mm});
            skCircle(sketch, "E3.10.8.1", {"center": v(-111, 1) * mm, "radius": 1 * mm});
            skCircle(sketch, "E3.10.9.0", {"center": v(-121, -9) * mm, "radius": 1 * mm});
            skCircle(sketch, "E3.10.9.1", {"center": v(-111, -19) * mm, "radius": 1 * mm});
            skCircle(sketch, "E3.10.10.0", {"center": v(-121, -29) * mm, "radius": 1 * mm});
            skCircle(sketch, "E3.10.10.1", {"center": v(-111, -39) * mm, "radius": 1 * mm});
            skCircle(sketch, "E3.10.11.0", {"center": v(-121, -49) * mm, "radius": 1 * mm});
            skCircle(sketch, "E3.10.11.1", {"center": v(-111, -59) * mm, "radius": 1 * mm});
            skCircle(sketch, "E3.10.12.0", {"center": v(-121, -69) * mm, "radius": 1 * mm});
            skCircle(sketch, "E3.10.12.1", {"center": v(-111, -79) * mm, "radius": 1 * mm});
            skCircle(sketch, "E3.10.13.0", {"center": v(-121, -89) * mm, "radius": 1 * mm});
            skCircle(sketch, "E3.10.13.1", {"center": v(-111, -99) * mm, "radius": 1 * mm});
            skCircle(sketch, "E3.10.14.0", {"center": v(-121, -109) * mm, "radius": 1 * mm});
            skCircle(sketch, "E3.10.14.1", {"center": v(-111, -119) * mm, "radius": 1 * mm});
            skCircle(sketch, "E3.10.15.0", {"center": v(-121, -129) * mm, "radius": 1 * mm});
            skCircle(sketch, "E3.10.15.1", {"center": v(-111, -139) * mm, "radius": 1 * mm});
            skCircle(sketch, "E3.10.16.0", {"center": v(-121, -149) * mm, "radius": 1 * mm});
            skCircle(sketch, "E3.10.16.1", {"center": v(-111, -159) * mm, "radius": 1 * mm});
            skCircle(sketch, "E3.10.17.0", {"center": v(-121, -169) * mm, "radius": 1 * mm});
            skCircle(sketch, "E3.10.17.1", {"center": v(-111, -179) * mm, "radius": 1 * mm, "construction": true});
            skCircle(sketch, "E3.11.0.0", {"center": v(-101, 171) * mm, "radius": 1 * mm});
            skCircle(sketch, "E3.11.0.1", {"center": v(-91, 161) * mm, "radius": 1 * mm});
            skCircle(sketch, "E3.11.1.0", {"center": v(-101, 151) * mm, "radius": 1 * mm});
            skCircle(sketch, "E3.11.1.1", {"center": v(-91, 141) * mm, "radius": 1 * mm});
            skCircle(sketch, "E3.11.2.0", {"center": v(-101, 131) * mm, "radius": 1 * mm});
            skCircle(sketch, "E3.11.2.1", {"center": v(-91, 121) * mm, "radius": 1 * mm});
            skCircle(sketch, "E3.11.3.0", {"center": v(-101, 111) * mm, "radius": 1 * mm});
            skCircle(sketch, "E3.11.3.1", {"center": v(-91, 101) * mm, "radius": 1 * mm});
            skCircle(sketch, "E3.11.4.0", {"center": v(-101, 91) * mm, "radius": 1 * mm});
            skCircle(sketch, "E3.11.4.1", {"center": v(-91, 81) * mm, "radius": 1 * mm});
            skCircle(sketch, "E3.11.5.0", {"center": v(-101, 71) * mm, "radius": 1 * mm});
            skCircle(sketch, "E3.11.5.1", {"center": v(-91, 61) * mm, "radius": 1 * mm});
            skCircle(sketch, "E3.11.6.0", {"center": v(-101, 51) * mm, "radius": 1 * mm});
            skCircle(sketch, "E3.11.6.1", {"center": v(-91, 41) * mm, "radius": 1 * mm});
            skCircle(sketch, "E3.11.7.0", {"center": v(-101, 31) * mm, "radius": 1 * mm});
            skCircle(sketch, "E3.11.7.1", {"center": v(-91, 21) * mm, "radius": 1 * mm});
            skCircle(sketch, "E3.11.8.0", {"center": v(-101, 11) * mm, "radius": 1 * mm});
            skCircle(sketch, "E3.11.8.1", {"center": v(-91, 1) * mm, "radius": 1 * mm});
            skCircle(sketch, "E3.11.9.0", {"center": v(-101, -9) * mm, "radius": 1 * mm});
            skCircle(sketch, "E3.11.9.1", {"center": v(-91, -19) * mm, "radius": 1 * mm});
            skCircle(sketch, "E3.11.10.0", {"center": v(-101, -29) * mm, "radius": 1 * mm});
            skCircle(sketch, "E3.11.10.1", {"center": v(-91, -39) * mm, "radius": 1 * mm});
            skCircle(sketch, "E3.11.11.0", {"center": v(-101, -49) * mm, "radius": 1 * mm});
            skCircle(sketch, "E3.11.11.1", {"center": v(-91, -59) * mm, "radius": 1 * mm});
            skCircle(sketch, "E3.11.12.0", {"center": v(-101, -69) * mm, "radius": 1 * mm});
            skCircle(sketch, "E3.11.12.1", {"center": v(-91, -79) * mm, "radius": 1 * mm});
            skCircle(sketch, "E3.11.13.0", {"center": v(-101, -89) * mm, "radius": 1 * mm});
            skCircle(sketch, "E3.11.13.1", {"center": v(-91, -99) * mm, "radius": 1 * mm});
            skCircle(sketch, "E3.11.14.0", {"center": v(-101, -109) * mm, "radius": 1 * mm});
            skCircle(sketch, "E3.11.14.1", {"center": v(-91, -119) * mm, "radius": 1 * mm});
            skCircle(sketch, "E3.11.15.0", {"center": v(-101, -129) * mm, "radius": 1 * mm});
            skCircle(sketch, "E3.11.15.1", {"center": v(-91, -139) * mm, "radius": 1 * mm});
            skCircle(sketch, "E3.11.16.0", {"center": v(-101, -149) * mm, "radius": 1 * mm});
            skCircle(sketch, "E3.11.16.1", {"center": v(-91, -159) * mm, "radius": 1 * mm});
            skCircle(sketch, "E3.11.17.0", {"center": v(-101, -169) * mm, "radius": 1 * mm});
            skCircle(sketch, "E3.11.17.1", {"center": v(-91, -179) * mm, "radius": 1 * mm, "construction": true});
            skCircle(sketch, "E3.12.0.0", {"center": v(-81, 171) * mm, "radius": 1 * mm});
            skCircle(sketch, "E3.12.0.1", {"center": v(-71, 161) * mm, "radius": 1 * mm});
            skCircle(sketch, "E3.12.1.0", {"center": v(-81, 151) * mm, "radius": 1 * mm});
            skCircle(sketch, "E3.12.1.1", {"center": v(-71, 141) * mm, "radius": 1 * mm});
            skCircle(sketch, "E3.12.2.0", {"center": v(-81, 131) * mm, "radius": 1 * mm});
            skCircle(sketch, "E3.12.2.1", {"center": v(-71, 121) * mm, "radius": 1 * mm});
            skCircle(sketch, "E3.12.3.0", {"center": v(-81, 111) * mm, "radius": 1 * mm});
            skCircle(sketch, "E3.12.3.1", {"center": v(-71, 101) * mm, "radius": 1 * mm});
            skCircle(sketch, "E3.12.4.0", {"center": v(-81, 91) * mm, "radius": 1 * mm});
            skCircle(sketch, "E3.12.4.1", {"center": v(-71, 81) * mm, "radius": 1 * mm});
            skCircle(sketch, "E3.12.5.0", {"center": v(-81, 71) * mm, "radius": 1 * mm});
            skCircle(sketch, "E3.12.5.1", {"center": v(-71, 61) * mm, "radius": 1 * mm});
            skCircle(sketch, "E3.12.6.0", {"center": v(-81, 51) * mm, "radius": 1 * mm});
            skCircle(sketch, "E3.12.6.1", {"center": v(-71, 41) * mm, "radius": 1 * mm});
            skCircle(sketch, "E3.12.7.0", {"center": v(-81, 31) * mm, "radius": 1 * mm});
            skCircle(sketch, "E3.12.7.1", {"center": v(-71, 21) * mm, "radius": 1 * mm});
            skCircle(sketch, "E3.12.8.0", {"center": v(-81, 11) * mm, "radius": 1 * mm});
            skCircle(sketch, "E3.12.8.1", {"center": v(-71, 1) * mm, "radius": 1 * mm});
            skCircle(sketch, "E3.12.9.0", {"center": v(-81, -9) * mm, "radius": 1 * mm});
            skCircle(sketch, "E3.12.9.1", {"center": v(-71, -19) * mm, "radius": 1 * mm});
            skCircle(sketch, "E3.12.10.0", {"center": v(-81, -29) * mm, "radius": 1 * mm});
            skCircle(sketch, "E3.12.10.1", {"center": v(-71, -39) * mm, "radius": 1 * mm});
            skCircle(sketch, "E3.12.11.0", {"center": v(-81, -49) * mm, "radius": 1 * mm});
            skCircle(sketch, "E3.12.11.1", {"center": v(-71, -59) * mm, "radius": 1 * mm});
            skCircle(sketch, "E3.12.12.0", {"center": v(-81, -69) * mm, "radius": 1 * mm});
            skCircle(sketch, "E3.12.12.1", {"center": v(-71, -79) * mm, "radius": 1 * mm});
            skCircle(sketch, "E3.12.13.0", {"center": v(-81, -89) * mm, "radius": 1 * mm});
            skCircle(sketch, "E3.12.13.1", {"center": v(-71, -99) * mm, "radius": 1 * mm});
            skCircle(sketch, "E3.12.14.0", {"center": v(-81, -109) * mm, "radius": 1 * mm});
            skCircle(sketch, "E3.12.14.1", {"center": v(-71, -119) * mm, "radius": 1 * mm});
            skCircle(sketch, "E3.12.15.0", {"center": v(-81, -129) * mm, "radius": 1 * mm});
            skCircle(sketch, "E3.12.15.1", {"center": v(-71, -139) * mm, "radius": 1 * mm});
            skCircle(sketch, "E3.12.16.0", {"center": v(-81, -149) * mm, "radius": 1 * mm});
            skCircle(sketch, "E3.12.16.1", {"center": v(-71, -159) * mm, "radius": 1 * mm});
            skCircle(sketch, "E3.12.17.0", {"center": v(-81, -169) * mm, "radius": 1 * mm});
            skCircle(sketch, "E3.12.17.1", {"center": v(-71, -179) * mm, "radius": 1 * mm, "construction": true});
            skCircle(sketch, "E3.13.0.0", {"center": v(-61, 171) * mm, "radius": 1 * mm});
            skCircle(sketch, "E3.13.0.1", {"center": v(-51, 161) * mm, "radius": 1 * mm});
            skCircle(sketch, "E3.13.1.0", {"center": v(-61, 151) * mm, "radius": 1 * mm});
            skCircle(sketch, "E3.13.1.1", {"center": v(-51, 141) * mm, "radius": 1 * mm});
            skCircle(sketch, "E3.13.2.0", {"center": v(-61, 131) * mm, "radius": 1 * mm});
            skCircle(sketch, "E3.13.2.1", {"center": v(-51, 121) * mm, "radius": 1 * mm});
            skCircle(sketch, "E3.13.3.0", {"center": v(-61, 111) * mm, "radius": 1 * mm});
            skCircle(sketch, "E3.13.3.1", {"center": v(-51, 101) * mm, "radius": 1 * mm});
            skCircle(sketch, "E3.13.4.0", {"center": v(-61, 91) * mm, "radius": 1 * mm});
            skCircle(sketch, "E3.13.4.1", {"center": v(-51, 81) * mm, "radius": 1 * mm});
            skCircle(sketch, "E3.13.5.0", {"center": v(-61, 71) * mm, "radius": 1 * mm});
            skCircle(sketch, "E3.13.5.1", {"center": v(-51, 61) * mm, "radius": 1 * mm});
            skCircle(sketch, "E3.13.6.0", {"center": v(-61, 51) * mm, "radius": 1 * mm});
            skCircle(sketch, "E3.13.6.1", {"center": v(-51, 41) * mm, "radius": 1 * mm});
            skCircle(sketch, "E3.13.7.0", {"center": v(-61, 31) * mm, "radius": 1 * mm});
            skCircle(sketch, "E3.13.7.1", {"center": v(-51, 21) * mm, "radius": 1 * mm});
            skCircle(sketch, "E3.13.8.0", {"center": v(-61, 11) * mm, "radius": 1 * mm});
            skCircle(sketch, "E3.13.8.1", {"center": v(-51, 1) * mm, "radius": 1 * mm});
            skCircle(sketch, "E3.13.9.0", {"center": v(-61, -9) * mm, "radius": 1 * mm});
            skCircle(sketch, "E3.13.9.1", {"center": v(-51, -19) * mm, "radius": 1 * mm});
            skCircle(sketch, "E3.13.10.0", {"center": v(-61, -29) * mm, "radius": 1 * mm});
            skCircle(sketch, "E3.13.10.1", {"center": v(-51, -39) * mm, "radius": 1 * mm});
            skCircle(sketch, "E3.13.11.0", {"center": v(-61, -49) * mm, "radius": 1 * mm});
            skCircle(sketch, "E3.13.11.1", {"center": v(-51, -59) * mm, "radius": 1 * mm});
            skCircle(sketch, "E3.13.12.0", {"center": v(-61, -69) * mm, "radius": 1 * mm});
            skCircle(sketch, "E3.13.12.1", {"center": v(-51, -79) * mm, "radius": 1 * mm});
            skCircle(sketch, "E3.13.13.0", {"center": v(-61, -89) * mm, "radius": 1 * mm});
            skCircle(sketch, "E3.13.13.1", {"center": v(-51, -99) * mm, "radius": 1 * mm});
            skCircle(sketch, "E3.13.14.0", {"center": v(-61, -109) * mm, "radius": 1 * mm});
            skCircle(sketch, "E3.13.14.1", {"center": v(-51, -119) * mm, "radius": 1 * mm});
            skCircle(sketch, "E3.13.15.0", {"center": v(-61, -129) * mm, "radius": 1 * mm});
            skCircle(sketch, "E3.13.15.1", {"center": v(-51, -139) * mm, "radius": 1 * mm});
            skCircle(sketch, "E3.13.16.0", {"center": v(-61, -149) * mm, "radius": 1 * mm});
            skCircle(sketch, "E3.13.16.1", {"center": v(-51, -159) * mm, "radius": 1 * mm});
            skCircle(sketch, "E3.13.17.0", {"center": v(-61, -169) * mm, "radius": 1 * mm});
            skCircle(sketch, "E3.13.17.1", {"center": v(-51, -179) * mm, "radius": 1 * mm, "construction": true});
            skCircle(sketch, "E3.14.0.0", {"center": v(-41, 171) * mm, "radius": 1 * mm});
            skCircle(sketch, "E3.14.0.1", {"center": v(-31, 161) * mm, "radius": 1 * mm});
            skCircle(sketch, "E3.14.1.0", {"center": v(-41, 151) * mm, "radius": 1 * mm});
            skCircle(sketch, "E3.14.1.1", {"center": v(-31, 141) * mm, "radius": 1 * mm});
            skCircle(sketch, "E3.14.2.0", {"center": v(-41, 131) * mm, "radius": 1 * mm});
            skCircle(sketch, "E3.14.2.1", {"center": v(-31, 121) * mm, "radius": 1 * mm});
            skCircle(sketch, "E3.14.3.0", {"center": v(-41, 111) * mm, "radius": 1 * mm});
            skCircle(sketch, "E3.14.3.1", {"center": v(-31, 101) * mm, "radius": 1 * mm});
            skCircle(sketch, "E3.14.4.0", {"center": v(-41, 91) * mm, "radius": 1 * mm});
            skCircle(sketch, "E3.14.4.1", {"center": v(-31, 81) * mm, "radius": 1 * mm});
            skCircle(sketch, "E3.14.5.0", {"center": v(-41, 71) * mm, "radius": 1 * mm});
            skCircle(sketch, "E3.14.5.1", {"center": v(-31, 61) * mm, "radius": 1 * mm});
            skCircle(sketch, "E3.14.6.0", {"center": v(-41, 51) * mm, "radius": 1 * mm});
            skCircle(sketch, "E3.14.6.1", {"center": v(-31, 41) * mm, "radius": 1 * mm});
            skCircle(sketch, "E3.14.7.0", {"center": v(-41, 31) * mm, "radius": 1 * mm});
            skCircle(sketch, "E3.14.7.1", {"center": v(-31, 21) * mm, "radius": 1 * mm});
            skCircle(sketch, "E3.14.8.0", {"center": v(-41, 11) * mm, "radius": 1 * mm});
            skCircle(sketch, "E3.14.8.1", {"center": v(-31, 1) * mm, "radius": 1 * mm});
            skCircle(sketch, "E3.14.9.0", {"center": v(-41, -9) * mm, "radius": 1 * mm});
            skCircle(sketch, "E3.14.9.1", {"center": v(-31, -19) * mm, "radius": 1 * mm});
            skCircle(sketch, "E3.14.10.0", {"center": v(-41, -29) * mm, "radius": 1 * mm});
            skCircle(sketch, "E3.14.10.1", {"center": v(-31, -39) * mm, "radius": 1 * mm});
            skCircle(sketch, "E3.14.11.0", {"center": v(-41, -49) * mm, "radius": 1 * mm});
            skCircle(sketch, "E3.14.11.1", {"center": v(-31, -59) * mm, "radius": 1 * mm});
            skCircle(sketch, "E3.14.12.0", {"center": v(-41, -69) * mm, "radius": 1 * mm});
            skCircle(sketch, "E3.14.12.1", {"center": v(-31, -79) * mm, "radius": 1 * mm});
            skCircle(sketch, "E3.14.13.0", {"center": v(-41, -89) * mm, "radius": 1 * mm});
            skCircle(sketch, "E3.14.13.1", {"center": v(-31, -99) * mm, "radius": 1 * mm});
            skCircle(sketch, "E3.14.14.0", {"center": v(-41, -109) * mm, "radius": 1 * mm});
            skCircle(sketch, "E3.14.14.1", {"center": v(-31, -119) * mm, "radius": 1 * mm});
            skCircle(sketch, "E3.14.15.0", {"center": v(-41, -129) * mm, "radius": 1 * mm});
            skCircle(sketch, "E3.14.15.1", {"center": v(-31, -139) * mm, "radius": 1 * mm});
            skCircle(sketch, "E3.14.16.0", {"center": v(-41, -149) * mm, "radius": 1 * mm});
            skCircle(sketch, "E3.14.16.1", {"center": v(-31, -159) * mm, "radius": 1 * mm});
            skCircle(sketch, "E3.14.17.0", {"center": v(-41, -169) * mm, "radius": 1 * mm});
            skCircle(sketch, "E3.14.17.1", {"center": v(-31, -179) * mm, "radius": 1 * mm, "construction": true});
            skCircle(sketch, "E3.15.0.0", {"center": v(-21, 171) * mm, "radius": 1 * mm});
            skCircle(sketch, "E3.15.0.1", {"center": v(-11, 161) * mm, "radius": 1 * mm});
            skCircle(sketch, "E3.15.1.0", {"center": v(-21, 151) * mm, "radius": 1 * mm});
            skCircle(sketch, "E3.15.1.1", {"center": v(-11, 141) * mm, "radius": 1 * mm});
            skCircle(sketch, "E3.15.2.0", {"center": v(-21, 131) * mm, "radius": 1 * mm});
            skCircle(sketch, "E3.15.2.1", {"center": v(-11, 121) * mm, "radius": 1 * mm});
            skCircle(sketch, "E3.15.3.0", {"center": v(-21, 111) * mm, "radius": 1 * mm});
            skCircle(sketch, "E3.15.3.1", {"center": v(-11, 101) * mm, "radius": 1 * mm});
            skCircle(sketch, "E3.15.4.0", {"center": v(-21, 91) * mm, "radius": 1 * mm});
            skCircle(sketch, "E3.15.4.1", {"center": v(-11, 81) * mm, "radius": 1 * mm});
            skCircle(sketch, "E3.15.5.0", {"center": v(-21, 71) * mm, "radius": 1 * mm});
            skCircle(sketch, "E3.15.5.1", {"center": v(-11, 61) * mm, "radius": 1 * mm});
            skCircle(sketch, "E3.15.6.0", {"center": v(-21, 51) * mm, "radius": 1 * mm});
            skCircle(sketch, "E3.15.6.1", {"center": v(-11, 41) * mm, "radius": 1 * mm});
            skCircle(sketch, "E3.15.7.0", {"center": v(-21, 31) * mm, "radius": 1 * mm});
            skCircle(sketch, "E3.15.7.1", {"center": v(-11, 21) * mm, "radius": 1 * mm});
            skCircle(sketch, "E3.15.8.0", {"center": v(-21, 11) * mm, "radius": 1 * mm});
            skCircle(sketch, "E3.15.8.1", {"center": v(-11, 1) * mm, "radius": 1 * mm});
            skCircle(sketch, "E3.15.9.0", {"center": v(-21, -9) * mm, "radius": 1 * mm});
            skCircle(sketch, "E3.15.9.1", {"center": v(-11, -19) * mm, "radius": 1 * mm});
            skCircle(sketch, "E3.15.10.0", {"center": v(-21, -29) * mm, "radius": 1 * mm});
            skCircle(sketch, "E3.15.10.1", {"center": v(-11, -39) * mm, "radius": 1 * mm});
            skCircle(sketch, "E3.15.11.0", {"center": v(-21, -49) * mm, "radius": 1 * mm});
            skCircle(sketch, "E3.15.11.1", {"center": v(-11, -59) * mm, "radius": 1 * mm});
            skCircle(sketch, "E3.15.12.0", {"center": v(-21, -69) * mm, "radius": 1 * mm});
            skCircle(sketch, "E3.15.12.1", {"center": v(-11, -79) * mm, "radius": 1 * mm});
            skCircle(sketch, "E3.15.13.0", {"center": v(-21, -89) * mm, "radius": 1 * mm});
            skCircle(sketch, "E3.15.13.1", {"center": v(-11, -99) * mm, "radius": 1 * mm});
            skCircle(sketch, "E3.15.14.0", {"center": v(-21, -109) * mm, "radius": 1 * mm});
            skCircle(sketch, "E3.15.14.1", {"center": v(-11, -119) * mm, "radius": 1 * mm});
            skCircle(sketch, "E3.15.15.0", {"center": v(-21, -129) * mm, "radius": 1 * mm});
            skCircle(sketch, "E3.15.15.1", {"center": v(-11, -139) * mm, "radius": 1 * mm});
            skCircle(sketch, "E3.15.16.0", {"center": v(-21, -149) * mm, "radius": 1 * mm});
            skCircle(sketch, "E3.15.16.1", {"center": v(-11, -159) * mm, "radius": 1 * mm});
            skCircle(sketch, "E3.15.17.0", {"center": v(-21, -169) * mm, "radius": 1 * mm});
            skCircle(sketch, "E3.15.17.1", {"center": v(-11, -179) * mm, "radius": 1 * mm, "construction": true});
            skCircle(sketch, "E3.16.0.0", {"center": v(-1, 171) * mm, "radius": 1 * mm});
            skCircle(sketch, "E3.16.0.1", {"center": v(9, 161) * mm, "radius": 1 * mm});
            skCircle(sketch, "E3.16.1.0", {"center": v(-1, 151) * mm, "radius": 1 * mm});
            skCircle(sketch, "E3.16.1.1", {"center": v(9, 141) * mm, "radius": 1 * mm});
            skCircle(sketch, "E3.16.2.0", {"center": v(-1, 131) * mm, "radius": 1 * mm});
            skCircle(sketch, "E3.16.2.1", {"center": v(9, 121) * mm, "radius": 1 * mm});
            skCircle(sketch, "E3.16.3.0", {"center": v(-1, 111) * mm, "radius": 1 * mm});
            skCircle(sketch, "E3.16.3.1", {"center": v(9, 101) * mm, "radius": 1 * mm});
            skCircle(sketch, "E3.16.4.0", {"center": v(-1, 91) * mm, "radius": 1 * mm});
            skCircle(sketch, "E3.16.4.1", {"center": v(9, 81) * mm, "radius": 1 * mm});
            skCircle(sketch, "E3.16.5.0", {"center": v(-1, 71) * mm, "radius": 1 * mm});
            skCircle(sketch, "E3.16.5.1", {"center": v(9, 61) * mm, "radius": 1 * mm});
            skCircle(sketch, "E3.16.6.0", {"center": v(-1, 51) * mm, "radius": 1 * mm});
            skCircle(sketch, "E3.16.6.1", {"center": v(9, 41) * mm, "radius": 1 * mm});
            skCircle(sketch, "E3.16.7.0", {"center": v(-1, 31) * mm, "radius": 1 * mm});
            skCircle(sketch, "E3.16.7.1", {"center": v(9, 21) * mm, "radius": 1 * mm});
            skCircle(sketch, "E3.16.8.0", {"center": v(-1, 11) * mm, "radius": 1 * mm});
            skCircle(sketch, "E3.16.8.1", {"center": v(9, 1) * mm, "radius": 1 * mm});
            skCircle(sketch, "E3.16.9.0", {"center": v(-1, -9) * mm, "radius": 1 * mm});
            skCircle(sketch, "E3.16.9.1", {"center": v(9, -19) * mm, "radius": 1 * mm});
            skCircle(sketch, "E3.16.10.0", {"center": v(-1, -29) * mm, "radius": 1 * mm});
            skCircle(sketch, "E3.16.10.1", {"center": v(9, -39) * mm, "radius": 1 * mm});
            skCircle(sketch, "E3.16.11.0", {"center": v(-1, -49) * mm, "radius": 1 * mm});
            skCircle(sketch, "E3.16.11.1", {"center": v(9, -59) * mm, "radius": 1 * mm});
            skCircle(sketch, "E3.16.12.0", {"center": v(-1, -69) * mm, "radius": 1 * mm});
            skCircle(sketch, "E3.16.12.1", {"center": v(9, -79) * mm, "radius": 1 * mm});
            skCircle(sketch, "E3.16.13.0", {"center": v(-1, -89) * mm, "radius": 1 * mm});
            skCircle(sketch, "E3.16.13.1", {"center": v(9, -99) * mm, "radius": 1 * mm});
            skCircle(sketch, "E3.16.14.0", {"center": v(-1, -109) * mm, "radius": 1 * mm});
            skCircle(sketch, "E3.16.14.1", {"center": v(9, -119) * mm, "radius": 1 * mm});
            skCircle(sketch, "E3.16.15.0", {"center": v(-1, -129) * mm, "radius": 1 * mm});
            skCircle(sketch, "E3.16.15.1", {"center": v(9, -139) * mm, "radius": 1 * mm});
            skCircle(sketch, "E3.16.16.0", {"center": v(-1, -149) * mm, "radius": 1 * mm});
            skCircle(sketch, "E3.16.16.1", {"center": v(9, -159) * mm, "radius": 1 * mm});
            skCircle(sketch, "E3.16.17.0", {"center": v(-1, -169) * mm, "radius": 1 * mm});
            skCircle(sketch, "E3.16.17.1", {"center": v(9, -179) * mm, "radius": 1 * mm, "construction": true});
            skCircle(sketch, "E3.17.0.0", {"center": v(19, 171) * mm, "radius": 1 * mm});
            skCircle(sketch, "E3.17.0.1", {"center": v(29, 161) * mm, "radius": 1 * mm});
            skCircle(sketch, "E3.17.1.0", {"center": v(19, 151) * mm, "radius": 1 * mm});
            skCircle(sketch, "E3.17.1.1", {"center": v(29, 141) * mm, "radius": 1 * mm});
            skCircle(sketch, "E3.17.2.0", {"center": v(19, 131) * mm, "radius": 1 * mm});
            skCircle(sketch, "E3.17.2.1", {"center": v(29, 121) * mm, "radius": 1 * mm});
            skCircle(sketch, "E3.17.3.0", {"center": v(19, 111) * mm, "radius": 1 * mm});
            skCircle(sketch, "E3.17.3.1", {"center": v(29, 101) * mm, "radius": 1 * mm});
            skCircle(sketch, "E3.17.4.0", {"center": v(19, 91) * mm, "radius": 1 * mm});
            skCircle(sketch, "E3.17.4.1", {"center": v(29, 81) * mm, "radius": 1 * mm});
            skCircle(sketch, "E3.17.5.0", {"center": v(19, 71) * mm, "radius": 1 * mm});
            skCircle(sketch, "E3.17.5.1", {"center": v(29, 61) * mm, "radius": 1 * mm});
            skCircle(sketch, "E3.17.6.0", {"center": v(19, 51) * mm, "radius": 1 * mm});
            skCircle(sketch, "E3.17.6.1", {"center": v(29, 41) * mm, "radius": 1 * mm});
            skCircle(sketch, "E3.17.7.0", {"center": v(19, 31) * mm, "radius": 1 * mm});
            skCircle(sketch, "E3.17.7.1", {"center": v(29, 21) * mm, "radius": 1 * mm});
            skCircle(sketch, "E3.17.8.0", {"center": v(19, 11) * mm, "radius": 1 * mm});
            skCircle(sketch, "E3.17.8.1", {"center": v(29, 1) * mm, "radius": 1 * mm});
            skCircle(sketch, "E3.17.9.0", {"center": v(19, -9) * mm, "radius": 1 * mm});
            skCircle(sketch, "E3.17.9.1", {"center": v(29, -19) * mm, "radius": 1 * mm});
            skCircle(sketch, "E3.17.10.0", {"center": v(19, -29) * mm, "radius": 1 * mm});
            skCircle(sketch, "E3.17.10.1", {"center": v(29, -39) * mm, "radius": 1 * mm});
            skCircle(sketch, "E3.17.11.0", {"center": v(19, -49) * mm, "radius": 1 * mm});
            skCircle(sketch, "E3.17.11.1", {"center": v(29, -59) * mm, "radius": 1 * mm});
            skCircle(sketch, "E3.17.12.0", {"center": v(19, -69) * mm, "radius": 1 * mm});
            skCircle(sketch, "E3.17.12.1", {"center": v(29, -79) * mm, "radius": 1 * mm});
            skCircle(sketch, "E3.17.13.0", {"center": v(19, -89) * mm, "radius": 1 * mm});
            skCircle(sketch, "E3.17.13.1", {"center": v(29, -99) * mm, "radius": 1 * mm});
            skCircle(sketch, "E3.17.14.0", {"center": v(19, -109) * mm, "radius": 1 * mm});
            skCircle(sketch, "E3.17.14.1", {"center": v(29, -119) * mm, "radius": 1 * mm});
            skCircle(sketch, "E3.17.15.0", {"center": v(19, -129) * mm, "radius": 1 * mm});
            skCircle(sketch, "E3.17.15.1", {"center": v(29, -139) * mm, "radius": 1 * mm});
            skCircle(sketch, "E3.17.16.0", {"center": v(19, -149) * mm, "radius": 1 * mm});
            skCircle(sketch, "E3.17.16.1", {"center": v(29, -159) * mm, "radius": 1 * mm});
            skCircle(sketch, "E3.17.17.0", {"center": v(19, -169) * mm, "radius": 1 * mm});
            skCircle(sketch, "E3.17.17.1", {"center": v(29, -179) * mm, "radius": 1 * mm, "construction": true});
            skCircle(sketch, "E3.18.0.0", {"center": v(39, 171) * mm, "radius": 1 * mm});
            skCircle(sketch, "E3.18.0.1", {"center": v(49, 161) * mm, "radius": 1 * mm});
            skCircle(sketch, "E3.18.1.0", {"center": v(39, 151) * mm, "radius": 1 * mm});
            skCircle(sketch, "E3.18.1.1", {"center": v(49, 141) * mm, "radius": 1 * mm});
            skCircle(sketch, "E3.18.2.0", {"center": v(39, 131) * mm, "radius": 1 * mm});
            skCircle(sketch, "E3.18.2.1", {"center": v(49, 121) * mm, "radius": 1 * mm});
            skCircle(sketch, "E3.18.3.0", {"center": v(39, 111) * mm, "radius": 1 * mm});
            skCircle(sketch, "E3.18.3.1", {"center": v(49, 101) * mm, "radius": 1 * mm});
            skCircle(sketch, "E3.18.4.0", {"center": v(39, 91) * mm, "radius": 1 * mm});
            skCircle(sketch, "E3.18.4.1", {"center": v(49, 81) * mm, "radius": 1 * mm});
            skCircle(sketch, "E3.18.5.0", {"center": v(39, 71) * mm, "radius": 1 * mm});
            skCircle(sketch, "E3.18.5.1", {"center": v(49, 61) * mm, "radius": 1 * mm});
            skCircle(sketch, "E3.18.6.0", {"center": v(39, 51) * mm, "radius": 1 * mm});
            skCircle(sketch, "E3.18.6.1", {"center": v(49, 41) * mm, "radius": 1 * mm});
            skCircle(sketch, "E3.18.7.0", {"center": v(39, 31) * mm, "radius": 1 * mm});
            skCircle(sketch, "E3.18.7.1", {"center": v(49, 21) * mm, "radius": 1 * mm});
            skCircle(sketch, "E3.18.8.0", {"center": v(39, 11) * mm, "radius": 1 * mm});
            skCircle(sketch, "E3.18.8.1", {"center": v(49, 1) * mm, "radius": 1 * mm});
            skCircle(sketch, "E3.18.9.0", {"center": v(39, -9) * mm, "radius": 1 * mm});
            skCircle(sketch, "E3.18.9.1", {"center": v(49, -19) * mm, "radius": 1 * mm});
            skCircle(sketch, "E3.18.10.0", {"center": v(39, -29) * mm, "radius": 1 * mm});
            skCircle(sketch, "E3.18.10.1", {"center": v(49, -39) * mm, "radius": 1 * mm});
            skCircle(sketch, "E3.18.11.0", {"center": v(39, -49) * mm, "radius": 1 * mm});
            skCircle(sketch, "E3.18.11.1", {"center": v(49, -59) * mm, "radius": 1 * mm});
            skCircle(sketch, "E3.18.12.0", {"center": v(39, -69) * mm, "radius": 1 * mm});
            skCircle(sketch, "E3.18.12.1", {"center": v(49, -79) * mm, "radius": 1 * mm});
            skCircle(sketch, "E3.18.13.0", {"center": v(39, -89) * mm, "radius": 1 * mm});
            skCircle(sketch, "E3.18.13.1", {"center": v(49, -99) * mm, "radius": 1 * mm});
            skCircle(sketch, "E3.18.14.0", {"center": v(39, -109) * mm, "radius": 1 * mm});
            skCircle(sketch, "E3.18.14.1", {"center": v(49, -119) * mm, "radius": 1 * mm});
            skCircle(sketch, "E3.18.15.0", {"center": v(39, -129) * mm, "radius": 1 * mm});
            skCircle(sketch, "E3.18.15.1", {"center": v(49, -139) * mm, "radius": 1 * mm});
            skCircle(sketch, "E3.18.16.0", {"center": v(39, -149) * mm, "radius": 1 * mm});
            skCircle(sketch, "E3.18.16.1", {"center": v(49, -159) * mm, "radius": 1 * mm});
            skCircle(sketch, "E3.18.17.0", {"center": v(39, -169) * mm, "radius": 1 * mm});
            skCircle(sketch, "E3.18.17.1", {"center": v(49, -179) * mm, "radius": 1 * mm, "construction": true});
            skCircle(sketch, "E3.19.0.0", {"center": v(59, 171) * mm, "radius": 1 * mm});
            skCircle(sketch, "E3.19.0.1", {"center": v(69, 161) * mm, "radius": 1 * mm});
            skCircle(sketch, "E3.19.1.0", {"center": v(59, 151) * mm, "radius": 1 * mm});
            skCircle(sketch, "E3.19.1.1", {"center": v(69, 141) * mm, "radius": 1 * mm});
            skCircle(sketch, "E3.19.2.0", {"center": v(59, 131) * mm, "radius": 1 * mm});
            skCircle(sketch, "E3.19.2.1", {"center": v(69, 121) * mm, "radius": 1 * mm});
            skCircle(sketch, "E3.19.3.0", {"center": v(59, 111) * mm, "radius": 1 * mm});
            skCircle(sketch, "E3.19.3.1", {"center": v(69, 101) * mm, "radius": 1 * mm});
            skCircle(sketch, "E3.19.4.0", {"center": v(59, 91) * mm, "radius": 1 * mm});
            skCircle(sketch, "E3.19.4.1", {"center": v(69, 81) * mm, "radius": 1 * mm});
            skCircle(sketch, "E3.19.5.0", {"center": v(59, 71) * mm, "radius": 1 * mm});
            skCircle(sketch, "E3.19.5.1", {"center": v(69, 61) * mm, "radius": 1 * mm});
            skCircle(sketch, "E3.19.6.0", {"center": v(59, 51) * mm, "radius": 1 * mm});
            skCircle(sketch, "E3.19.6.1", {"center": v(69, 41) * mm, "radius": 1 * mm});
            skCircle(sketch, "E3.19.7.0", {"center": v(59, 31) * mm, "radius": 1 * mm});
            skCircle(sketch, "E3.19.7.1", {"center": v(69, 21) * mm, "radius": 1 * mm});
            skCircle(sketch, "E3.19.8.0", {"center": v(59, 11) * mm, "radius": 1 * mm});
            skCircle(sketch, "E3.19.8.1", {"center": v(69, 1) * mm, "radius": 1 * mm});
            skCircle(sketch, "E3.19.9.0", {"center": v(59, -9) * mm, "radius": 1 * mm});
            skCircle(sketch, "E3.19.9.1", {"center": v(69, -19) * mm, "radius": 1 * mm});
            skCircle(sketch, "E3.19.10.0", {"center": v(59, -29) * mm, "radius": 1 * mm});
            skCircle(sketch, "E3.19.10.1", {"center": v(69, -39) * mm, "radius": 1 * mm});
            skCircle(sketch, "E3.19.11.0", {"center": v(59, -49) * mm, "radius": 1 * mm});
            skCircle(sketch, "E3.19.11.1", {"center": v(69, -59) * mm, "radius": 1 * mm});
            skCircle(sketch, "E3.19.12.0", {"center": v(59, -69) * mm, "radius": 1 * mm});
            skCircle(sketch, "E3.19.12.1", {"center": v(69, -79) * mm, "radius": 1 * mm});
            skCircle(sketch, "E3.19.13.0", {"center": v(59, -89) * mm, "radius": 1 * mm});
            skCircle(sketch, "E3.19.13.1", {"center": v(69, -99) * mm, "radius": 1 * mm});
            skCircle(sketch, "E3.19.14.0", {"center": v(59, -109) * mm, "radius": 1 * mm});
            skCircle(sketch, "E3.19.14.1", {"center": v(69, -119) * mm, "radius": 1 * mm});
            skCircle(sketch, "E3.19.15.0", {"center": v(59, -129) * mm, "radius": 1 * mm});
            skCircle(sketch, "E3.19.15.1", {"center": v(69, -139) * mm, "radius": 1 * mm});
            skCircle(sketch, "E3.19.16.0", {"center": v(59, -149) * mm, "radius": 1 * mm});
            skCircle(sketch, "E3.19.16.1", {"center": v(69, -159) * mm, "radius": 1 * mm});
            skCircle(sketch, "E3.19.17.0", {"center": v(59, -169) * mm, "radius": 1 * mm});
            skCircle(sketch, "E3.19.17.1", {"center": v(69, -179) * mm, "radius": 1 * mm, "construction": true});
            skCircle(sketch, "E3.20.0.0", {"center": v(79, 171) * mm, "radius": 1 * mm});
            skCircle(sketch, "E3.20.0.1", {"center": v(89, 161) * mm, "radius": 1 * mm});
            skCircle(sketch, "E3.20.1.0", {"center": v(79, 151) * mm, "radius": 1 * mm});
            skCircle(sketch, "E3.20.1.1", {"center": v(89, 141) * mm, "radius": 1 * mm});
            skCircle(sketch, "E3.20.2.0", {"center": v(79, 131) * mm, "radius": 1 * mm});
            skCircle(sketch, "E3.20.2.1", {"center": v(89, 121) * mm, "radius": 1 * mm});
            skCircle(sketch, "E3.20.3.0", {"center": v(79, 111) * mm, "radius": 1 * mm});
            skCircle(sketch, "E3.20.3.1", {"center": v(89, 101) * mm, "radius": 1 * mm});
            skCircle(sketch, "E3.20.4.0", {"center": v(79, 91) * mm, "radius": 1 * mm});
            skCircle(sketch, "E3.20.4.1", {"center": v(89, 81) * mm, "radius": 1 * mm});
            skCircle(sketch, "E3.20.5.0", {"center": v(79, 71) * mm, "radius": 1 * mm});
            skCircle(sketch, "E3.20.5.1", {"center": v(89, 61) * mm, "radius": 1 * mm});
            skCircle(sketch, "E3.20.6.0", {"center": v(79, 51) * mm, "radius": 1 * mm});
            skCircle(sketch, "E3.20.6.1", {"center": v(89, 41) * mm, "radius": 1 * mm});
            skCircle(sketch, "E3.20.7.0", {"center": v(79, 31) * mm, "radius": 1 * mm});
            skCircle(sketch, "E3.20.7.1", {"center": v(89, 21) * mm, "radius": 1 * mm});
            skCircle(sketch, "E3.20.8.0", {"center": v(79, 11) * mm, "radius": 1 * mm});
            skCircle(sketch, "E3.20.8.1", {"center": v(89, 1) * mm, "radius": 1 * mm});
            skCircle(sketch, "E3.20.9.0", {"center": v(79, -9) * mm, "radius": 1 * mm});
            skCircle(sketch, "E3.20.9.1", {"center": v(89, -19) * mm, "radius": 1 * mm});
            skCircle(sketch, "E3.20.10.0", {"center": v(79, -29) * mm, "radius": 1 * mm});
            skCircle(sketch, "E3.20.10.1", {"center": v(89, -39) * mm, "radius": 1 * mm});
            skCircle(sketch, "E3.20.11.0", {"center": v(79, -49) * mm, "radius": 1 * mm});
            skCircle(sketch, "E3.20.11.1", {"center": v(89, -59) * mm, "radius": 1 * mm});
            skCircle(sketch, "E3.20.12.0", {"center": v(79, -69) * mm, "radius": 1 * mm});
            skCircle(sketch, "E3.20.12.1", {"center": v(89, -79) * mm, "radius": 1 * mm});
            skCircle(sketch, "E3.20.13.0", {"center": v(79, -89) * mm, "radius": 1 * mm});
            skCircle(sketch, "E3.20.13.1", {"center": v(89, -99) * mm, "radius": 1 * mm});
            skCircle(sketch, "E3.20.14.0", {"center": v(79, -109) * mm, "radius": 1 * mm});
            skCircle(sketch, "E3.20.14.1", {"center": v(89, -119) * mm, "radius": 1 * mm});
            skCircle(sketch, "E3.20.15.0", {"center": v(79, -129) * mm, "radius": 1 * mm});
            skCircle(sketch, "E3.20.15.1", {"center": v(89, -139) * mm, "radius": 1 * mm});
            skCircle(sketch, "E3.20.16.0", {"center": v(79, -149) * mm, "radius": 1 * mm});
            skCircle(sketch, "E3.20.16.1", {"center": v(89, -159) * mm, "radius": 1 * mm});
            skCircle(sketch, "E3.20.17.0", {"center": v(79, -169) * mm, "radius": 1 * mm});
            skCircle(sketch, "E3.20.17.1", {"center": v(89, -179) * mm, "radius": 1 * mm, "construction": true});
            skCircle(sketch, "E3.21.0.0", {"center": v(99, 171) * mm, "radius": 1 * mm});
            skCircle(sketch, "E3.21.0.1", {"center": v(109, 161) * mm, "radius": 1 * mm});
            skCircle(sketch, "E3.21.1.0", {"center": v(99, 151) * mm, "radius": 1 * mm});
            skCircle(sketch, "E3.21.1.1", {"center": v(109, 141) * mm, "radius": 1 * mm});
            skCircle(sketch, "E3.21.2.0", {"center": v(99, 131) * mm, "radius": 1 * mm});
            skCircle(sketch, "E3.21.2.1", {"center": v(109, 121) * mm, "radius": 1 * mm});
            skCircle(sketch, "E3.21.3.0", {"center": v(99, 111) * mm, "radius": 1 * mm});
            skCircle(sketch, "E3.21.3.1", {"center": v(109, 101) * mm, "radius": 1 * mm});
            skCircle(sketch, "E3.21.4.0", {"center": v(99, 91) * mm, "radius": 1 * mm});
            skCircle(sketch, "E3.21.4.1", {"center": v(109, 81) * mm, "radius": 1 * mm});
            skCircle(sketch, "E3.21.5.0", {"center": v(99, 71) * mm, "radius": 1 * mm});
            skCircle(sketch, "E3.21.5.1", {"center": v(109, 61) * mm, "radius": 1 * mm});
            skCircle(sketch, "E3.21.6.0", {"center": v(99, 51) * mm, "radius": 1 * mm});
            skCircle(sketch, "E3.21.6.1", {"center": v(109, 41) * mm, "radius": 1 * mm});
            skCircle(sketch, "E3.21.7.0", {"center": v(99, 31) * mm, "radius": 1 * mm});
            skCircle(sketch, "E3.21.7.1", {"center": v(109, 21) * mm, "radius": 1 * mm});
            skCircle(sketch, "E3.21.8.0", {"center": v(99, 11) * mm, "radius": 1 * mm});
            skCircle(sketch, "E3.21.8.1", {"center": v(109, 1) * mm, "radius": 1 * mm});
            skCircle(sketch, "E3.21.9.0", {"center": v(99, -9) * mm, "radius": 1 * mm});
            skCircle(sketch, "E3.21.9.1", {"center": v(109, -19) * mm, "radius": 1 * mm});
            skCircle(sketch, "E3.21.10.0", {"center": v(99, -29) * mm, "radius": 1 * mm});
            skCircle(sketch, "E3.21.10.1", {"center": v(109, -39) * mm, "radius": 1 * mm});
            skCircle(sketch, "E3.21.11.0", {"center": v(99, -49) * mm, "radius": 1 * mm});
            skCircle(sketch, "E3.21.11.1", {"center": v(109, -59) * mm, "radius": 1 * mm});
            skCircle(sketch, "E3.21.12.0", {"center": v(99, -69) * mm, "radius": 1 * mm});
            skCircle(sketch, "E3.21.12.1", {"center": v(109, -79) * mm, "radius": 1 * mm});
            skCircle(sketch, "E3.21.13.0", {"center": v(99, -89) * mm, "radius": 1 * mm});
            skCircle(sketch, "E3.21.13.1", {"center": v(109, -99) * mm, "radius": 1 * mm});
            skCircle(sketch, "E3.21.14.0", {"center": v(99, -109) * mm, "radius": 1 * mm});
            skCircle(sketch, "E3.21.14.1", {"center": v(109, -119) * mm, "radius": 1 * mm});
            skCircle(sketch, "E3.21.15.0", {"center": v(99, -129) * mm, "radius": 1 * mm});
            skCircle(sketch, "E3.21.15.1", {"center": v(109, -139) * mm, "radius": 1 * mm});
            skCircle(sketch, "E3.21.16.0", {"center": v(99, -149) * mm, "radius": 1 * mm});
            skCircle(sketch, "E3.21.16.1", {"center": v(109, -159) * mm, "radius": 1 * mm});
            skCircle(sketch, "E3.21.17.0", {"center": v(99, -169) * mm, "radius": 1 * mm});
            skCircle(sketch, "E3.21.17.1", {"center": v(109, -179) * mm, "radius": 1 * mm, "construction": true});
            skCircle(sketch, "E3.22.0.0", {"center": v(119, 171) * mm, "radius": 1 * mm});
            skCircle(sketch, "E3.22.0.1", {"center": v(129, 161) * mm, "radius": 1 * mm});
            skCircle(sketch, "E3.22.1.0", {"center": v(119, 151) * mm, "radius": 1 * mm});
            skCircle(sketch, "E3.22.1.1", {"center": v(129, 141) * mm, "radius": 1 * mm});
            skCircle(sketch, "E3.22.2.0", {"center": v(119, 131) * mm, "radius": 1 * mm});
            skCircle(sketch, "E3.22.2.1", {"center": v(129, 121) * mm, "radius": 1 * mm});
            skCircle(sketch, "E3.22.3.0", {"center": v(119, 111) * mm, "radius": 1 * mm});
            skCircle(sketch, "E3.22.3.1", {"center": v(129, 101) * mm, "radius": 1 * mm});
            skCircle(sketch, "E3.22.4.0", {"center": v(119, 91) * mm, "radius": 1 * mm});
            skCircle(sketch, "E3.22.4.1", {"center": v(129, 81) * mm, "radius": 1 * mm});
            skCircle(sketch, "E3.22.5.0", {"center": v(119, 71) * mm, "radius": 1 * mm});
            skCircle(sketch, "E3.22.5.1", {"center": v(129, 61) * mm, "radius": 1 * mm});
            skCircle(sketch, "E3.22.6.0", {"center": v(119, 51) * mm, "radius": 1 * mm});
            skCircle(sketch, "E3.22.6.1", {"center": v(129, 41) * mm, "radius": 1 * mm});
            skCircle(sketch, "E3.22.7.0", {"center": v(119, 31) * mm, "radius": 1 * mm});
            skCircle(sketch, "E3.22.7.1", {"center": v(129, 21) * mm, "radius": 1 * mm});
            skCircle(sketch, "E3.22.8.0", {"center": v(119, 11) * mm, "radius": 1 * mm});
            skCircle(sketch, "E3.22.8.1", {"center": v(129, 1) * mm, "radius": 1 * mm});
            skCircle(sketch, "E3.22.9.0", {"center": v(119, -9) * mm, "radius": 1 * mm});
            skCircle(sketch, "E3.22.9.1", {"center": v(129, -19) * mm, "radius": 1 * mm});
            skCircle(sketch, "E3.22.10.0", {"center": v(119, -29) * mm, "radius": 1 * mm});
            skCircle(sketch, "E3.22.10.1", {"center": v(129, -39) * mm, "radius": 1 * mm});
            skCircle(sketch, "E3.22.11.0", {"center": v(119, -49) * mm, "radius": 1 * mm});
            skCircle(sketch, "E3.22.11.1", {"center": v(129, -59) * mm, "radius": 1 * mm});
            skCircle(sketch, "E3.22.12.0", {"center": v(119, -69) * mm, "radius": 1 * mm});
            skCircle(sketch, "E3.22.12.1", {"center": v(129, -79) * mm, "radius": 1 * mm});
            skCircle(sketch, "E3.22.13.0", {"center": v(119, -89) * mm, "radius": 1 * mm});
            skCircle(sketch, "E3.22.13.1", {"center": v(129, -99) * mm, "radius": 1 * mm});
            skCircle(sketch, "E3.22.14.0", {"center": v(119, -109) * mm, "radius": 1 * mm});
            skCircle(sketch, "E3.22.14.1", {"center": v(129, -119) * mm, "radius": 1 * mm});
            skCircle(sketch, "E3.22.15.0", {"center": v(119, -129) * mm, "radius": 1 * mm});
            skCircle(sketch, "E3.22.15.1", {"center": v(129, -139) * mm, "radius": 1 * mm});
            skCircle(sketch, "E3.22.16.0", {"center": v(119, -149) * mm, "radius": 1 * mm});
            skCircle(sketch, "E3.22.16.1", {"center": v(129, -159) * mm, "radius": 1 * mm});
            skCircle(sketch, "E3.22.17.0", {"center": v(119, -169) * mm, "radius": 1 * mm});
            skCircle(sketch, "E3.22.17.1", {"center": v(129, -179) * mm, "radius": 1 * mm, "construction": true});
            skCircle(sketch, "E3.23.0.0", {"center": v(139, 171) * mm, "radius": 1 * mm});
            skCircle(sketch, "E3.23.0.1", {"center": v(149, 161) * mm, "radius": 1 * mm});
            skCircle(sketch, "E3.23.1.0", {"center": v(139, 151) * mm, "radius": 1 * mm});
            skCircle(sketch, "E3.23.1.1", {"center": v(149, 141) * mm, "radius": 1 * mm});
            skCircle(sketch, "E3.23.2.0", {"center": v(139, 131) * mm, "radius": 1 * mm});
            skCircle(sketch, "E3.23.2.1", {"center": v(149, 121) * mm, "radius": 1 * mm});
            skCircle(sketch, "E3.23.3.0", {"center": v(139, 111) * mm, "radius": 1 * mm});
            skCircle(sketch, "E3.23.3.1", {"center": v(149, 101) * mm, "radius": 1 * mm});
            skCircle(sketch, "E3.23.4.0", {"center": v(139, 91) * mm, "radius": 1 * mm});
            skCircle(sketch, "E3.23.4.1", {"center": v(149, 81) * mm, "radius": 1 * mm});
            skCircle(sketch, "E3.23.5.0", {"center": v(139, 71) * mm, "radius": 1 * mm});
            skCircle(sketch, "E3.23.5.1", {"center": v(149, 61) * mm, "radius": 1 * mm});
            skCircle(sketch, "E3.23.6.0", {"center": v(139, 51) * mm, "radius": 1 * mm});
            skCircle(sketch, "E3.23.6.1", {"center": v(149, 41) * mm, "radius": 1 * mm});
            skCircle(sketch, "E3.23.7.0", {"center": v(139, 31) * mm, "radius": 1 * mm});
            skCircle(sketch, "E3.23.7.1", {"center": v(149, 21) * mm, "radius": 1 * mm});
            skCircle(sketch, "E3.23.8.0", {"center": v(139, 11) * mm, "radius": 1 * mm});
            skCircle(sketch, "E3.23.8.1", {"center": v(149, 1) * mm, "radius": 1 * mm});
            skCircle(sketch, "E3.23.9.0", {"center": v(139, -9) * mm, "radius": 1 * mm});
            skCircle(sketch, "E3.23.9.1", {"center": v(149, -19) * mm, "radius": 1 * mm});
            skCircle(sketch, "E3.23.10.0", {"center": v(139, -29) * mm, "radius": 1 * mm});
            skCircle(sketch, "E3.23.10.1", {"center": v(149, -39) * mm, "radius": 1 * mm});
            skCircle(sketch, "E3.23.11.0", {"center": v(139, -49) * mm, "radius": 1 * mm});
            skCircle(sketch, "E3.23.11.1", {"center": v(149, -59) * mm, "radius": 1 * mm});
            skCircle(sketch, "E3.23.12.0", {"center": v(139, -69) * mm, "radius": 1 * mm});
            skCircle(sketch, "E3.23.12.1", {"center": v(149, -79) * mm, "radius": 1 * mm});
            skCircle(sketch, "E3.23.13.0", {"center": v(139, -89) * mm, "radius": 1 * mm});
            skCircle(sketch, "E3.23.13.1", {"center": v(149, -99) * mm, "radius": 1 * mm});
            skCircle(sketch, "E3.23.14.0", {"center": v(139, -109) * mm, "radius": 1 * mm});
            skCircle(sketch, "E3.23.14.1", {"center": v(149, -119) * mm, "radius": 1 * mm});
            skCircle(sketch, "E3.23.15.0", {"center": v(139, -129) * mm, "radius": 1 * mm});
            skCircle(sketch, "E3.23.15.1", {"center": v(149, -139) * mm, "radius": 1 * mm});
            skCircle(sketch, "E3.23.16.0", {"center": v(139, -149) * mm, "radius": 1 * mm});
            skCircle(sketch, "E3.23.16.1", {"center": v(149, -159) * mm, "radius": 1 * mm});
            skCircle(sketch, "E3.23.17.0", {"center": v(139, -169) * mm, "radius": 1 * mm});
            skCircle(sketch, "E3.23.17.1", {"center": v(149, -179) * mm, "radius": 1 * mm, "construction": true});
            skCircle(sketch, "E3.24.0.0", {"center": v(159, 171) * mm, "radius": 1 * mm});
            skCircle(sketch, "E3.24.0.1", {"center": v(169, 161) * mm, "radius": 1 * mm});
            skCircle(sketch, "E3.24.1.0", {"center": v(159, 151) * mm, "radius": 1 * mm});
            skCircle(sketch, "E3.24.1.1", {"center": v(169, 141) * mm, "radius": 1 * mm});
            skCircle(sketch, "E3.24.2.0", {"center": v(159, 131) * mm, "radius": 1 * mm});
            skCircle(sketch, "E3.24.2.1", {"center": v(169, 121) * mm, "radius": 1 * mm});
            skCircle(sketch, "E3.24.3.0", {"center": v(159, 111) * mm, "radius": 1 * mm});
            skCircle(sketch, "E3.24.3.1", {"center": v(169, 101) * mm, "radius": 1 * mm});
            skCircle(sketch, "E3.24.4.0", {"center": v(159, 91) * mm, "radius": 1 * mm});
            skCircle(sketch, "E3.24.4.1", {"center": v(169, 81) * mm, "radius": 1 * mm});
            skCircle(sketch, "E3.24.5.0", {"center": v(159, 71) * mm, "radius": 1 * mm});
            skCircle(sketch, "E3.24.5.1", {"center": v(169, 61) * mm, "radius": 1 * mm});
            skCircle(sketch, "E3.24.6.0", {"center": v(159, 51) * mm, "radius": 1 * mm});
            skCircle(sketch, "E3.24.6.1", {"center": v(169, 41) * mm, "radius": 1 * mm});
            skCircle(sketch, "E3.24.7.0", {"center": v(159, 31) * mm, "radius": 1 * mm});
            skCircle(sketch, "E3.24.7.1", {"center": v(169, 21) * mm, "radius": 1 * mm});
            skCircle(sketch, "E3.24.8.0", {"center": v(159, 11) * mm, "radius": 1 * mm});
            skCircle(sketch, "E3.24.8.1", {"center": v(169, 1) * mm, "radius": 1 * mm});
            skCircle(sketch, "E3.24.9.0", {"center": v(159, -9) * mm, "radius": 1 * mm});
            skCircle(sketch, "E3.24.9.1", {"center": v(169, -19) * mm, "radius": 1 * mm});
            skCircle(sketch, "E3.24.10.0", {"center": v(159, -29) * mm, "radius": 1 * mm});
            skCircle(sketch, "E3.24.10.1", {"center": v(169, -39) * mm, "radius": 1 * mm});
            skCircle(sketch, "E3.24.11.0", {"center": v(159, -49) * mm, "radius": 1 * mm});
            skCircle(sketch, "E3.24.11.1", {"center": v(169, -59) * mm, "radius": 1 * mm});
            skCircle(sketch, "E3.24.12.0", {"center": v(159, -69) * mm, "radius": 1 * mm});
            skCircle(sketch, "E3.24.12.1", {"center": v(169, -79) * mm, "radius": 1 * mm});
            skCircle(sketch, "E3.24.13.0", {"center": v(159, -89) * mm, "radius": 1 * mm});
            skCircle(sketch, "E3.24.13.1", {"center": v(169, -99) * mm, "radius": 1 * mm});
            skCircle(sketch, "E3.24.14.0", {"center": v(159, -109) * mm, "radius": 1 * mm});
            skCircle(sketch, "E3.24.14.1", {"center": v(169, -119) * mm, "radius": 1 * mm});
            skCircle(sketch, "E3.24.15.0", {"center": v(159, -129) * mm, "radius": 1 * mm});
            skCircle(sketch, "E3.24.15.1", {"center": v(169, -139) * mm, "radius": 1 * mm});
            skCircle(sketch, "E3.24.16.0", {"center": v(159, -149) * mm, "radius": 1 * mm});
            skCircle(sketch, "E3.24.16.1", {"center": v(169, -159) * mm, "radius": 1 * mm});
            skCircle(sketch, "E3.24.17.0", {"center": v(159, -169) * mm, "radius": 1 * mm});
            skCircle(sketch, "E3.24.17.1", {"center": v(169, -179) * mm, "radius": 1 * mm, "construction": true});
            skCircle(sketch, "E3.25.0.0", {"center": v(179, 171) * mm, "radius": 1 * mm});
            skCircle(sketch, "E3.25.0.1", {"center": v(189, 161) * mm, "radius": 1 * mm});
            skCircle(sketch, "E3.25.1.0", {"center": v(179, 151) * mm, "radius": 1 * mm});
            skCircle(sketch, "E3.25.1.1", {"center": v(189, 141) * mm, "radius": 1 * mm});
            skCircle(sketch, "E3.25.2.0", {"center": v(179, 131) * mm, "radius": 1 * mm});
            skCircle(sketch, "E3.25.2.1", {"center": v(189, 121) * mm, "radius": 1 * mm});
            skCircle(sketch, "E3.25.3.0", {"center": v(179, 111) * mm, "radius": 1 * mm});
            skCircle(sketch, "E3.25.3.1", {"center": v(189, 101) * mm, "radius": 1 * mm});
            skCircle(sketch, "E3.25.4.0", {"center": v(179, 91) * mm, "radius": 1 * mm});
            skCircle(sketch, "E3.25.4.1", {"center": v(189, 81) * mm, "radius": 1 * mm});
            skCircle(sketch, "E3.25.5.0", {"center": v(179, 71) * mm, "radius": 1 * mm});
            skCircle(sketch, "E3.25.5.1", {"center": v(189, 61) * mm, "radius": 1 * mm});
            skCircle(sketch, "E3.25.6.0", {"center": v(179, 51) * mm, "radius": 1 * mm});
            skCircle(sketch, "E3.25.6.1", {"center": v(189, 41) * mm, "radius": 1 * mm});
            skCircle(sketch, "E3.25.7.0", {"center": v(179, 31) * mm, "radius": 1 * mm});
            skCircle(sketch, "E3.25.7.1", {"center": v(189, 21) * mm, "radius": 1 * mm});
            skCircle(sketch, "E3.25.8.0", {"center": v(179, 11) * mm, "radius": 1 * mm});
            skCircle(sketch, "E3.25.8.1", {"center": v(189, 1) * mm, "radius": 1 * mm});
            skCircle(sketch, "E3.25.9.0", {"center": v(179, -9) * mm, "radius": 1 * mm});
            skCircle(sketch, "E3.25.9.1", {"center": v(189, -19) * mm, "radius": 1 * mm});
            skCircle(sketch, "E3.25.10.0", {"center": v(179, -29) * mm, "radius": 1 * mm});
            skCircle(sketch, "E3.25.10.1", {"center": v(189, -39) * mm, "radius": 1 * mm});
            skCircle(sketch, "E3.25.11.0", {"center": v(179, -49) * mm, "radius": 1 * mm});
            skCircle(sketch, "E3.25.11.1", {"center": v(189, -59) * mm, "radius": 1 * mm});
            skCircle(sketch, "E3.25.12.0", {"center": v(179, -69) * mm, "radius": 1 * mm});
            skCircle(sketch, "E3.25.12.1", {"center": v(189, -79) * mm, "radius": 1 * mm});
            skCircle(sketch, "E3.25.13.0", {"center": v(179, -89) * mm, "radius": 1 * mm});
            skCircle(sketch, "E3.25.13.1", {"center": v(189, -99) * mm, "radius": 1 * mm});
            skCircle(sketch, "E3.25.14.0", {"center": v(179, -109) * mm, "radius": 1 * mm});
            skCircle(sketch, "E3.25.14.1", {"center": v(189, -119) * mm, "radius": 1 * mm});
            skCircle(sketch, "E3.25.15.0", {"center": v(179, -129) * mm, "radius": 1 * mm});
            skCircle(sketch, "E3.25.15.1", {"center": v(189, -139) * mm, "radius": 1 * mm});
            skCircle(sketch, "E3.25.16.0", {"center": v(179, -149) * mm, "radius": 1 * mm});
            skCircle(sketch, "E3.25.16.1", {"center": v(189, -159) * mm, "radius": 1 * mm});
            skCircle(sketch, "E3.25.17.0", {"center": v(179, -169) * mm, "radius": 1 * mm});
            skCircle(sketch, "E3.25.17.1", {"center": v(189, -179) * mm, "radius": 1 * mm, "construction": true});
            skCircle(sketch, "E3.26.0.0", {"center": v(199, 171) * mm, "radius": 1 * mm});
            skCircle(sketch, "E3.26.0.1", {"center": v(209, 161) * mm, "radius": 1 * mm});
            skCircle(sketch, "E3.26.1.0", {"center": v(199, 151) * mm, "radius": 1 * mm});
            skCircle(sketch, "E3.26.1.1", {"center": v(209, 141) * mm, "radius": 1 * mm});
            skCircle(sketch, "E3.26.2.0", {"center": v(199, 131) * mm, "radius": 1 * mm});
            skCircle(sketch, "E3.26.2.1", {"center": v(209, 121) * mm, "radius": 1 * mm});
            skCircle(sketch, "E3.26.3.0", {"center": v(199, 111) * mm, "radius": 1 * mm});
            skCircle(sketch, "E3.26.3.1", {"center": v(209, 101) * mm, "radius": 1 * mm});
            skCircle(sketch, "E3.26.4.0", {"center": v(199, 91) * mm, "radius": 1 * mm});
            skCircle(sketch, "E3.26.4.1", {"center": v(209, 81) * mm, "radius": 1 * mm});
            skCircle(sketch, "E3.26.5.0", {"center": v(199, 71) * mm, "radius": 1 * mm});
            skCircle(sketch, "E3.26.5.1", {"center": v(209, 61) * mm, "radius": 1 * mm});
            skCircle(sketch, "E3.26.6.0", {"center": v(199, 51) * mm, "radius": 1 * mm});
            skCircle(sketch, "E3.26.6.1", {"center": v(209, 41) * mm, "radius": 1 * mm});
            skCircle(sketch, "E3.26.7.0", {"center": v(199, 31) * mm, "radius": 1 * mm});
            skCircle(sketch, "E3.26.7.1", {"center": v(209, 21) * mm, "radius": 1 * mm});
            skCircle(sketch, "E3.26.8.0", {"center": v(199, 11) * mm, "radius": 1 * mm});
            skCircle(sketch, "E3.26.8.1", {"center": v(209, 1) * mm, "radius": 1 * mm});
            skCircle(sketch, "E3.26.9.0", {"center": v(199, -9) * mm, "radius": 1 * mm});
            skCircle(sketch, "E3.26.9.1", {"center": v(209, -19) * mm, "radius": 1 * mm});
            skCircle(sketch, "E3.26.10.0", {"center": v(199, -29) * mm, "radius": 1 * mm});
            skCircle(sketch, "E3.26.10.1", {"center": v(209, -39) * mm, "radius": 1 * mm});
            skCircle(sketch, "E3.26.11.0", {"center": v(199, -49) * mm, "radius": 1 * mm});
            skCircle(sketch, "E3.26.11.1", {"center": v(209, -59) * mm, "radius": 1 * mm});
            skCircle(sketch, "E3.26.12.0", {"center": v(199, -69) * mm, "radius": 1 * mm});
            skCircle(sketch, "E3.26.12.1", {"center": v(209, -79) * mm, "radius": 1 * mm});
            skCircle(sketch, "E3.26.13.0", {"center": v(199, -89) * mm, "radius": 1 * mm});
            skCircle(sketch, "E3.26.13.1", {"center": v(209, -99) * mm, "radius": 1 * mm});
            skCircle(sketch, "E3.26.14.0", {"center": v(199, -109) * mm, "radius": 1 * mm});
            skCircle(sketch, "E3.26.14.1", {"center": v(209, -119) * mm, "radius": 1 * mm});
            skCircle(sketch, "E3.26.15.0", {"center": v(199, -129) * mm, "radius": 1 * mm});
            skCircle(sketch, "E3.26.15.1", {"center": v(209, -139) * mm, "radius": 1 * mm});
            skCircle(sketch, "E3.26.16.0", {"center": v(199, -149) * mm, "radius": 1 * mm});
            skCircle(sketch, "E3.26.16.1", {"center": v(209, -159) * mm, "radius": 1 * mm});
            skCircle(sketch, "E3.26.17.0", {"center": v(199, -169) * mm, "radius": 1 * mm});
            skCircle(sketch, "E3.26.17.1", {"center": v(209, -179) * mm, "radius": 1 * mm, "construction": true});
            skCircle(sketch, "E3.27.0.0", {"center": v(219, 171) * mm, "radius": 1 * mm});
            skCircle(sketch, "E3.27.0.1", {"center": v(229, 161) * mm, "radius": 1 * mm});
            skCircle(sketch, "E3.27.1.0", {"center": v(219, 151) * mm, "radius": 1 * mm});
            skCircle(sketch, "E3.27.1.1", {"center": v(229, 141) * mm, "radius": 1 * mm});
            skCircle(sketch, "E3.27.2.0", {"center": v(219, 131) * mm, "radius": 1 * mm});
            skCircle(sketch, "E3.27.2.1", {"center": v(229, 121) * mm, "radius": 1 * mm});
            skCircle(sketch, "E3.27.3.0", {"center": v(219, 111) * mm, "radius": 1 * mm});
            skCircle(sketch, "E3.27.3.1", {"center": v(229, 101) * mm, "radius": 1 * mm});
            skCircle(sketch, "E3.27.4.0", {"center": v(219, 91) * mm, "radius": 1 * mm});
            skCircle(sketch, "E3.27.4.1", {"center": v(229, 81) * mm, "radius": 1 * mm});
            skCircle(sketch, "E3.27.5.0", {"center": v(219, 71) * mm, "radius": 1 * mm});
            skCircle(sketch, "E3.27.5.1", {"center": v(229, 61) * mm, "radius": 1 * mm});
            skCircle(sketch, "E3.27.6.0", {"center": v(219, 51) * mm, "radius": 1 * mm});
            skCircle(sketch, "E3.27.6.1", {"center": v(229, 41) * mm, "radius": 1 * mm});
            skCircle(sketch, "E3.27.7.0", {"center": v(219, 31) * mm, "radius": 1 * mm});
            skCircle(sketch, "E3.27.7.1", {"center": v(229, 21) * mm, "radius": 1 * mm});
            skCircle(sketch, "E3.27.8.0", {"center": v(219, 11) * mm, "radius": 1 * mm});
            skCircle(sketch, "E3.27.8.1", {"center": v(229, 1) * mm, "radius": 1 * mm});
            skCircle(sketch, "E3.27.9.0", {"center": v(219, -9) * mm, "radius": 1 * mm});
            skCircle(sketch, "E3.27.9.1", {"center": v(229, -19) * mm, "radius": 1 * mm});
            skCircle(sketch, "E3.27.10.0", {"center": v(219, -29) * mm, "radius": 1 * mm});
            skCircle(sketch, "E3.27.10.1", {"center": v(229, -39) * mm, "radius": 1 * mm});
            skCircle(sketch, "E3.27.11.0", {"center": v(219, -49) * mm, "radius": 1 * mm});
            skCircle(sketch, "E3.27.11.1", {"center": v(229, -59) * mm, "radius": 1 * mm});
            skCircle(sketch, "E3.27.12.0", {"center": v(219, -69) * mm, "radius": 1 * mm});
            skCircle(sketch, "E3.27.12.1", {"center": v(229, -79) * mm, "radius": 1 * mm});
            skCircle(sketch, "E3.27.13.0", {"center": v(219, -89) * mm, "radius": 1 * mm});
            skCircle(sketch, "E3.27.13.1", {"center": v(229, -99) * mm, "radius": 1 * mm});
            skCircle(sketch, "E3.27.14.0", {"center": v(219, -109) * mm, "radius": 1 * mm});
            skCircle(sketch, "E3.27.14.1", {"center": v(229, -119) * mm, "radius": 1 * mm});
            skCircle(sketch, "E3.27.15.0", {"center": v(219, -129) * mm, "radius": 1 * mm});
            skCircle(sketch, "E3.27.15.1", {"center": v(229, -139) * mm, "radius": 1 * mm});
            skCircle(sketch, "E3.27.16.0", {"center": v(219, -149) * mm, "radius": 1 * mm});
            skCircle(sketch, "E3.27.16.1", {"center": v(229, -159) * mm, "radius": 1 * mm});
            skCircle(sketch, "E3.27.17.0", {"center": v(219, -169) * mm, "radius": 1 * mm});
            skCircle(sketch, "E3.27.17.1", {"center": v(229, -179) * mm, "radius": 1 * mm, "construction": true});
            skCircle(sketch, "E3.28.0.0", {"center": v(239, 171) * mm, "radius": 1 * mm});
            skCircle(sketch, "E3.28.0.1", {"center": v(249, 161) * mm, "radius": 1 * mm});
            skCircle(sketch, "E3.28.1.0", {"center": v(239, 151) * mm, "radius": 1 * mm});
            skCircle(sketch, "E3.28.1.1", {"center": v(249, 141) * mm, "radius": 1 * mm});
            skCircle(sketch, "E3.28.2.0", {"center": v(239, 131) * mm, "radius": 1 * mm});
            skCircle(sketch, "E3.28.2.1", {"center": v(249, 121) * mm, "radius": 1 * mm});
            skCircle(sketch, "E3.28.3.0", {"center": v(239, 111) * mm, "radius": 1 * mm});
            skCircle(sketch, "E3.28.3.1", {"center": v(249, 101) * mm, "radius": 1 * mm});
            skCircle(sketch, "E3.28.4.0", {"center": v(239, 91) * mm, "radius": 1 * mm});
            skCircle(sketch, "E3.28.4.1", {"center": v(249, 81) * mm, "radius": 1 * mm});
            skCircle(sketch, "E3.28.5.0", {"center": v(239, 71) * mm, "radius": 1 * mm});
            skCircle(sketch, "E3.28.5.1", {"center": v(249, 61) * mm, "radius": 1 * mm});
            skCircle(sketch, "E3.28.6.0", {"center": v(239, 51) * mm, "radius": 1 * mm});
            skCircle(sketch, "E3.28.6.1", {"center": v(249, 41) * mm, "radius": 1 * mm});
            skCircle(sketch, "E3.28.7.0", {"center": v(239, 31) * mm, "radius": 1 * mm});
            skCircle(sketch, "E3.28.7.1", {"center": v(249, 21) * mm, "radius": 1 * mm});
            skCircle(sketch, "E3.28.8.0", {"center": v(239, 11) * mm, "radius": 1 * mm});
            skCircle(sketch, "E3.28.8.1", {"center": v(249, 1) * mm, "radius": 1 * mm});
            skCircle(sketch, "E3.28.9.0", {"center": v(239, -9) * mm, "radius": 1 * mm});
            skCircle(sketch, "E3.28.9.1", {"center": v(249, -19) * mm, "radius": 1 * mm});
            skCircle(sketch, "E3.28.10.0", {"center": v(239, -29) * mm, "radius": 1 * mm});
            skCircle(sketch, "E3.28.10.1", {"center": v(249, -39) * mm, "radius": 1 * mm});
            skCircle(sketch, "E3.28.11.0", {"center": v(239, -49) * mm, "radius": 1 * mm});
            skCircle(sketch, "E3.28.11.1", {"center": v(249, -59) * mm, "radius": 1 * mm});
            skCircle(sketch, "E3.28.12.0", {"center": v(239, -69) * mm, "radius": 1 * mm});
            skCircle(sketch, "E3.28.12.1", {"center": v(249, -79) * mm, "radius": 1 * mm});
            skCircle(sketch, "E3.28.13.0", {"center": v(239, -89) * mm, "radius": 1 * mm});
            skCircle(sketch, "E3.28.13.1", {"center": v(249, -99) * mm, "radius": 1 * mm});
            skCircle(sketch, "E3.28.14.0", {"center": v(239, -109) * mm, "radius": 1 * mm});
            skCircle(sketch, "E3.28.14.1", {"center": v(249, -119) * mm, "radius": 1 * mm});
            skCircle(sketch, "E3.28.15.0", {"center": v(239, -129) * mm, "radius": 1 * mm});
            skCircle(sketch, "E3.28.15.1", {"center": v(249, -139) * mm, "radius": 1 * mm});
            skCircle(sketch, "E3.28.16.0", {"center": v(239, -149) * mm, "radius": 1 * mm});
            skCircle(sketch, "E3.28.16.1", {"center": v(249, -159) * mm, "radius": 1 * mm});
            skCircle(sketch, "E3.28.17.0", {"center": v(239, -169) * mm, "radius": 1 * mm});
            skCircle(sketch, "E3.28.17.1", {"center": v(249, -179) * mm, "radius": 1 * mm, "construction": true});
            skCircle(sketch, "E3.29.0.0", {"center": v(259, 171) * mm, "radius": 1 * mm});
            skCircle(sketch, "E3.29.0.1", {"center": v(269, 161) * mm, "radius": 1 * mm});
            skCircle(sketch, "E3.29.1.0", {"center": v(259, 151) * mm, "radius": 1 * mm});
            skCircle(sketch, "E3.29.1.1", {"center": v(269, 141) * mm, "radius": 1 * mm});
            skCircle(sketch, "E3.29.2.0", {"center": v(259, 131) * mm, "radius": 1 * mm});
            skCircle(sketch, "E3.29.2.1", {"center": v(269, 121) * mm, "radius": 1 * mm});
            skCircle(sketch, "E3.29.3.0", {"center": v(259, 111) * mm, "radius": 1 * mm});
            skCircle(sketch, "E3.29.3.1", {"center": v(269, 101) * mm, "radius": 1 * mm});
            skCircle(sketch, "E3.29.4.0", {"center": v(259, 91) * mm, "radius": 1 * mm});
            skCircle(sketch, "E3.29.4.1", {"center": v(269, 81) * mm, "radius": 1 * mm});
            skCircle(sketch, "E3.29.5.0", {"center": v(259, 71) * mm, "radius": 1 * mm});
            skCircle(sketch, "E3.29.5.1", {"center": v(269, 61) * mm, "radius": 1 * mm});
            skCircle(sketch, "E3.29.6.0", {"center": v(259, 51) * mm, "radius": 1 * mm});
            skCircle(sketch, "E3.29.6.1", {"center": v(269, 41) * mm, "radius": 1 * mm});
            skCircle(sketch, "E3.29.7.0", {"center": v(259, 31) * mm, "radius": 1 * mm});
            skCircle(sketch, "E3.29.7.1", {"center": v(269, 21) * mm, "radius": 1 * mm});
            skCircle(sketch, "E3.29.8.0", {"center": v(259, 11) * mm, "radius": 1 * mm});
            skCircle(sketch, "E3.29.8.1", {"center": v(269, 1) * mm, "radius": 1 * mm});
            skCircle(sketch, "E3.29.9.0", {"center": v(259, -9) * mm, "radius": 1 * mm});
            skCircle(sketch, "E3.29.9.1", {"center": v(269, -19) * mm, "radius": 1 * mm});
            skCircle(sketch, "E3.29.10.0", {"center": v(259, -29) * mm, "radius": 1 * mm});
            skCircle(sketch, "E3.29.10.1", {"center": v(269, -39) * mm, "radius": 1 * mm});
            skCircle(sketch, "E3.29.11.0", {"center": v(259, -49) * mm, "radius": 1 * mm});
            skCircle(sketch, "E3.29.11.1", {"center": v(269, -59) * mm, "radius": 1 * mm});
            skCircle(sketch, "E3.29.12.0", {"center": v(259, -69) * mm, "radius": 1 * mm});
            skCircle(sketch, "E3.29.12.1", {"center": v(269, -79) * mm, "radius": 1 * mm});
            skCircle(sketch, "E3.29.13.0", {"center": v(259, -89) * mm, "radius": 1 * mm});
            skCircle(sketch, "E3.29.13.1", {"center": v(269, -99) * mm, "radius": 1 * mm});
            skCircle(sketch, "E3.29.14.0", {"center": v(259, -109) * mm, "radius": 1 * mm});
            skCircle(sketch, "E3.29.14.1", {"center": v(269, -119) * mm, "radius": 1 * mm});
            skCircle(sketch, "E3.29.15.0", {"center": v(259, -129) * mm, "radius": 1 * mm});
            skCircle(sketch, "E3.29.15.1", {"center": v(269, -139) * mm, "radius": 1 * mm});
            skCircle(sketch, "E3.29.16.0", {"center": v(259, -149) * mm, "radius": 1 * mm});
            skCircle(sketch, "E3.29.16.1", {"center": v(269, -159) * mm, "radius": 1 * mm});
            skCircle(sketch, "E3.29.17.0", {"center": v(259, -169) * mm, "radius": 1 * mm});
            skCircle(sketch, "E3.29.17.1", {"center": v(269, -179) * mm, "radius": 1 * mm, "construction": true});
            skCircle(sketch, "E3.30.0.0", {"center": v(279, 171) * mm, "radius": 1 * mm});
            skCircle(sketch, "E3.30.0.1", {"center": v(289, 161) * mm, "radius": 1 * mm});
            skCircle(sketch, "E3.30.1.0", {"center": v(279, 151) * mm, "radius": 1 * mm});
            skCircle(sketch, "E3.30.1.1", {"center": v(289, 141) * mm, "radius": 1 * mm});
            skCircle(sketch, "E3.30.2.0", {"center": v(279, 131) * mm, "radius": 1 * mm});
            skCircle(sketch, "E3.30.2.1", {"center": v(289, 121) * mm, "radius": 1 * mm});
            skCircle(sketch, "E3.30.3.0", {"center": v(279, 111) * mm, "radius": 1 * mm});
            skCircle(sketch, "E3.30.3.1", {"center": v(289, 101) * mm, "radius": 1 * mm});
            skCircle(sketch, "E3.30.4.0", {"center": v(279, 91) * mm, "radius": 1 * mm});
            skCircle(sketch, "E3.30.4.1", {"center": v(289, 81) * mm, "radius": 1 * mm});
            skCircle(sketch, "E3.30.5.0", {"center": v(279, 71) * mm, "radius": 1 * mm});
            skCircle(sketch, "E3.30.5.1", {"center": v(289, 61) * mm, "radius": 1 * mm});
            skCircle(sketch, "E3.30.6.0", {"center": v(279, 51) * mm, "radius": 1 * mm});
            skCircle(sketch, "E3.30.6.1", {"center": v(289, 41) * mm, "radius": 1 * mm});
            skCircle(sketch, "E3.30.7.0", {"center": v(279, 31) * mm, "radius": 1 * mm});
            skCircle(sketch, "E3.30.7.1", {"center": v(289, 21) * mm, "radius": 1 * mm});
            skCircle(sketch, "E3.30.8.0", {"center": v(279, 11) * mm, "radius": 1 * mm});
            skCircle(sketch, "E3.30.8.1", {"center": v(289, 1) * mm, "radius": 1 * mm});
            skCircle(sketch, "E3.30.9.0", {"center": v(279, -9) * mm, "radius": 1 * mm});
            skCircle(sketch, "E3.30.9.1", {"center": v(289, -19) * mm, "radius": 1 * mm});
            skCircle(sketch, "E3.30.10.0", {"center": v(279, -29) * mm, "radius": 1 * mm});
            skCircle(sketch, "E3.30.10.1", {"center": v(289, -39) * mm, "radius": 1 * mm});
            skCircle(sketch, "E3.30.11.0", {"center": v(279, -49) * mm, "radius": 1 * mm});
            skCircle(sketch, "E3.30.11.1", {"center": v(289, -59) * mm, "radius": 1 * mm});
            skCircle(sketch, "E3.30.12.0", {"center": v(279, -69) * mm, "radius": 1 * mm});
            skCircle(sketch, "E3.30.12.1", {"center": v(289, -79) * mm, "radius": 1 * mm});
            skCircle(sketch, "E3.30.13.0", {"center": v(279, -89) * mm, "radius": 1 * mm});
            skCircle(sketch, "E3.30.13.1", {"center": v(289, -99) * mm, "radius": 1 * mm});
            skCircle(sketch, "E3.30.14.0", {"center": v(279, -109) * mm, "radius": 1 * mm});
            skCircle(sketch, "E3.30.14.1", {"center": v(289, -119) * mm, "radius": 1 * mm});
            skCircle(sketch, "E3.30.15.0", {"center": v(279, -129) * mm, "radius": 1 * mm});
            skCircle(sketch, "E3.30.15.1", {"center": v(289, -139) * mm, "radius": 1 * mm});
            skCircle(sketch, "E3.30.16.0", {"center": v(279, -149) * mm, "radius": 1 * mm});
            skCircle(sketch, "E3.30.16.1", {"center": v(289, -159) * mm, "radius": 1 * mm});
            skCircle(sketch, "E3.30.17.0", {"center": v(279, -169) * mm, "radius": 1 * mm});
            skCircle(sketch, "E3.30.17.1", {"center": v(289, -179) * mm, "radius": 1 * mm, "construction": true});
            skCircle(sketch, "E3.31.0.0", {"center": v(299, 171) * mm, "radius": 1 * mm});
            skCircle(sketch, "E3.31.0.1", {"center": v(309, 161) * mm, "radius": 1 * mm});
            skCircle(sketch, "E3.31.1.0", {"center": v(299, 151) * mm, "radius": 1 * mm});
            skCircle(sketch, "E3.31.1.1", {"center": v(309, 141) * mm, "radius": 1 * mm});
            skCircle(sketch, "E3.31.2.0", {"center": v(299, 131) * mm, "radius": 1 * mm});
            skCircle(sketch, "E3.31.2.1", {"center": v(309, 121) * mm, "radius": 1 * mm});
            skCircle(sketch, "E3.31.3.0", {"center": v(299, 111) * mm, "radius": 1 * mm});
            skCircle(sketch, "E3.31.3.1", {"center": v(309, 101) * mm, "radius": 1 * mm});
            skCircle(sketch, "E3.31.4.0", {"center": v(299, 91) * mm, "radius": 1 * mm});
            skCircle(sketch, "E3.31.4.1", {"center": v(309, 81) * mm, "radius": 1 * mm});
            skCircle(sketch, "E3.31.5.0", {"center": v(299, 71) * mm, "radius": 1 * mm});
            skCircle(sketch, "E3.31.5.1", {"center": v(309, 61) * mm, "radius": 1 * mm});
            skCircle(sketch, "E3.31.6.0", {"center": v(299, 51) * mm, "radius": 1 * mm});
            skCircle(sketch, "E3.31.6.1", {"center": v(309, 41) * mm, "radius": 1 * mm});
            skCircle(sketch, "E3.31.7.0", {"center": v(299, 31) * mm, "radius": 1 * mm});
            skCircle(sketch, "E3.31.7.1", {"center": v(309, 21) * mm, "radius": 1 * mm});
            skCircle(sketch, "E3.31.8.0", {"center": v(299, 11) * mm, "radius": 1 * mm});
            skCircle(sketch, "E3.31.8.1", {"center": v(309, 1) * mm, "radius": 1 * mm});
            skCircle(sketch, "E3.31.9.0", {"center": v(299, -9) * mm, "radius": 1 * mm});
            skCircle(sketch, "E3.31.9.1", {"center": v(309, -19) * mm, "radius": 1 * mm});
            skCircle(sketch, "E3.31.10.0", {"center": v(299, -29) * mm, "radius": 1 * mm});
            skCircle(sketch, "E3.31.10.1", {"center": v(309, -39) * mm, "radius": 1 * mm});
            skCircle(sketch, "E3.31.11.0", {"center": v(299, -49) * mm, "radius": 1 * mm});
            skCircle(sketch, "E3.31.11.1", {"center": v(309, -59) * mm, "radius": 1 * mm});
            skCircle(sketch, "E3.31.12.0", {"center": v(299, -69) * mm, "radius": 1 * mm});
            skCircle(sketch, "E3.31.12.1", {"center": v(309, -79) * mm, "radius": 1 * mm});
            skCircle(sketch, "E3.31.13.0", {"center": v(299, -89) * mm, "radius": 1 * mm});
            skCircle(sketch, "E3.31.13.1", {"center": v(309, -99) * mm, "radius": 1 * mm});
            skCircle(sketch, "E3.31.14.0", {"center": v(299, -109) * mm, "radius": 1 * mm});
            skCircle(sketch, "E3.31.14.1", {"center": v(309, -119) * mm, "radius": 1 * mm});
            skCircle(sketch, "E3.31.15.0", {"center": v(299, -129) * mm, "radius": 1 * mm});
            skCircle(sketch, "E3.31.15.1", {"center": v(309, -139) * mm, "radius": 1 * mm});
            skCircle(sketch, "E3.31.16.0", {"center": v(299, -149) * mm, "radius": 1 * mm});
            skCircle(sketch, "E3.31.16.1", {"center": v(309, -159) * mm, "radius": 1 * mm});
            skCircle(sketch, "E3.31.17.0", {"center": v(299, -169) * mm, "radius": 1 * mm});
            skCircle(sketch, "E3.31.17.1", {"center": v(309, -179) * mm, "radius": 1 * mm, "construction": true});
            skCircle(sketch, "E3.32.0.0", {"center": v(319, 171) * mm, "radius": 1 * mm});
            skCircle(sketch, "E3.32.0.1", {"center": v(329, 161) * mm, "radius": 1 * mm, "construction": true});
            skCircle(sketch, "E3.32.1.0", {"center": v(319, 151) * mm, "radius": 1 * mm});
            skCircle(sketch, "E3.32.1.1", {"center": v(329, 141) * mm, "radius": 1 * mm, "construction": true});
            skCircle(sketch, "E3.32.2.0", {"center": v(319, 131) * mm, "radius": 1 * mm});
            skCircle(sketch, "E3.32.2.1", {"center": v(329, 121) * mm, "radius": 1 * mm, "construction": true});
            skCircle(sketch, "E3.32.3.0", {"center": v(319, 111) * mm, "radius": 1 * mm});
            skCircle(sketch, "E3.32.3.1", {"center": v(329, 101) * mm, "radius": 1 * mm, "construction": true});
            skCircle(sketch, "E3.32.4.0", {"center": v(319, 91) * mm, "radius": 1 * mm});
            skCircle(sketch, "E3.32.4.1", {"center": v(329, 81) * mm, "radius": 1 * mm, "construction": true});
            skCircle(sketch, "E3.32.5.0", {"center": v(319, 71) * mm, "radius": 1 * mm});
            skCircle(sketch, "E3.32.5.1", {"center": v(329, 61) * mm, "radius": 1 * mm, "construction": true});
            skCircle(sketch, "E3.32.6.0", {"center": v(319, 51) * mm, "radius": 1 * mm});
            skCircle(sketch, "E3.32.6.1", {"center": v(329, 41) * mm, "radius": 1 * mm, "construction": true});
            skCircle(sketch, "E3.32.7.0", {"center": v(319, 31) * mm, "radius": 1 * mm});
            skCircle(sketch, "E3.32.7.1", {"center": v(329, 21) * mm, "radius": 1 * mm, "construction": true});
            skCircle(sketch, "E3.32.8.0", {"center": v(319, 11) * mm, "radius": 1 * mm});
            skCircle(sketch, "E3.32.8.1", {"center": v(329, 1) * mm, "radius": 1 * mm, "construction": true});
            skCircle(sketch, "E3.32.9.0", {"center": v(319, -9) * mm, "radius": 1 * mm});
            skCircle(sketch, "E3.32.9.1", {"center": v(329, -19) * mm, "radius": 1 * mm, "construction": true});
            skCircle(sketch, "E3.32.10.0", {"center": v(319, -29) * mm, "radius": 1 * mm});
            skCircle(sketch, "E3.32.10.1", {"center": v(329, -39) * mm, "radius": 1 * mm, "construction": true});
            skCircle(sketch, "E3.32.11.0", {"center": v(319, -49) * mm, "radius": 1 * mm});
            skCircle(sketch, "E3.32.11.1", {"center": v(329, -59) * mm, "radius": 1 * mm, "construction": true});
            skCircle(sketch, "E3.32.12.0", {"center": v(319, -69) * mm, "radius": 1 * mm});
            skCircle(sketch, "E3.32.12.1", {"center": v(329, -79) * mm, "radius": 1 * mm, "construction": true});
            skCircle(sketch, "E3.32.13.0", {"center": v(319, -89) * mm, "radius": 1 * mm});
            skCircle(sketch, "E3.32.13.1", {"center": v(329, -99) * mm, "radius": 1 * mm, "construction": true});
            skCircle(sketch, "E3.32.14.0", {"center": v(319, -109) * mm, "radius": 1 * mm});
            skCircle(sketch, "E3.32.14.1", {"center": v(329, -119) * mm, "radius": 1 * mm, "construction": true});
            skCircle(sketch, "E3.32.15.0", {"center": v(319, -129) * mm, "radius": 1 * mm});
            skCircle(sketch, "E3.32.15.1", {"center": v(329, -139) * mm, "radius": 1 * mm, "construction": true});
            skCircle(sketch, "E3.32.16.0", {"center": v(319, -149) * mm, "radius": 1 * mm});
            skCircle(sketch, "E3.32.16.1", {"center": v(329, -159) * mm, "radius": 1 * mm, "construction": true});
            skCircle(sketch, "E3.32.17.0", {"center": v(319, -169) * mm, "radius": 1 * mm});
            skCircle(sketch, "E3.32.17.1", {"center": v(329, -179) * mm, "radius": 1 * mm, "construction": true});
            skLineSegment(sketch, "E3.direction1", {"start": v(-311, 161) * mm, "end": v(-291, 161) * mm, "construction": true});
            skLineSegment(sketch, "E3.direction2", {"start": v(-311, 161) * mm, "end": v(-311, 141) * mm, "construction": true});
            skSolve(sketch);
        }
        {
            var Q0;
            Q0 = qSketchRegion(id + "F0", true);
            extrude(context, id + "F1", {"entities" : qUnion([Q0]), "depth" : 2 * mm, "offsetDistance" : 25 * mm});
        }
    });
